# Revit family: 879-002X7X-001-DN200-400
name_source: partatom
category: Pipe Accessories
units: mm (PartAtom-declared; Revit-internal decimal feet)

## family parameters
Always vertical = Yes
Cut with Voids When Loaded = No
Part Type = Valve - Breaks Into
Round Connector Dimension = Use Diameter
Shared = No
Work Plane-Based = No

## types (80) — shared parameters
879-0200-00-04400207299 = DN200_PN10
879-0200-00-044002072A0 = DN200_PN10
879-0200-00-04400217299 = DN200_PN10
879-0200-00-044002172A0 = DN200_PN10
879-0200-00-04400227299 = DN200_PN10
879-0200-00-044002272A0 = DN200_PN10
879-0200-00-04400237299 = DN200_PN10
879-0200-00-044002372A0 = DN200_PN10
879-0200-00-14400207299 = DN200_PN16
879-0200-00-144002072A0 = DN200_PN16
879-0200-00-14400217299 = DN200_PN16
879-0200-00-144002172A0 = DN200_PN16
879-0200-00-14400227299 = DN200_PN16
879-0200-00-144002272A0 = DN200_PN16
879-0200-00-14400237299 = DN200_PN16
879-0200-00-144002372A0 = DN200_PN16
879-0250-00-04400207299 = DN250_PN10
879-0250-00-044002072A0 = DN250_PN10
879-0250-00-04400217299 = DN250_PN10
879-0250-00-044002172A0 = DN250_PN10
879-0250-00-04400227299 = DN250_PN10
879-0250-00-044002272A0 = DN250_PN10
879-0250-00-04400237299 = DN250_PN10
879-0250-00-044002372A0 = DN250_PN16
879-0250-00-14400207299 = DN250_PN16
879-0250-00-144002072A0 = DN250_PN16
879-0250-00-14400217299 = DN250_PN16
879-0250-00-144002172A0 = DN250_PN16
879-0250-00-14400227299 = DN250_PN16
879-0250-00-144002272A0 = DN250_PN16
879-0250-00-14400237299 = DN250_PN16
879-0250-00-144002372A0 = DN250_PN16
879-0300-00-04400207299 = DN300_PN10
879-0300-00-044002072A0 = DN300_PN10
879-0300-00-04400217299 = DN300_PN10
879-0300-00-044002172A0 = DN300_PN10
879-0300-00-04400227299 = DN300_PN10
879-0300-00-044002272A0 = DN300_PN10
879-0300-00-04400237299 = DN300_PN10
879-0300-00-044002372A0 = DN300_PN10
879-0300-00-14400207299 = DN300_PN16
879-0300-00-144002072A0 = DN300_PN16
879-0300-00-14400217299 = DN300_PN16
879-0300-00-144002172A0 = DN300_PN16
879-0300-00-14400227299 = DN300_PN16
879-0300-00-144002272A0 = DN300_PN16
879-0300-00-14400237299 = DN300_PN16
879-0300-00-144002372A0 = DN300_PN16
879-0350-00-04400207299 = DN350_PN10
879-0350-00-044002072A0 = DN350_PN10
879-0350-00-04400217299 = DN350_PN10
879-0350-00-044002172A0 = DN350_PN10
879-0350-00-04400227299 = DN350_PN10
879-0350-00-044002272A0 = DN350_PN10
879-0350-00-04400237299 = DN350_PN10
879-0350-00-044002372A0 = DN350_PN10
879-0350-00-14400207299 = DN350_PN16
879-0350-00-144002072A0 = DN350_PN16
879-0350-00-14400217299 = DN350_PN16
879-0350-00-144002172A0 = DN350_PN16
879-0350-00-14400227299 = DN350_PN16
879-0350-00-144002272A0 = DN350_PN16
879-0350-00-14400237299 = DN350_PN16
879-0350-00-144002372A0 = DN350_PN16
879-0400-00-04400207299 = DN400_PN10
879-0400-00-044002072A0 = DN400_PN10
879-0400-00-04400217299 = DN400_PN10
879-0400-00-044002172A0 = DN400_PN10
879-0400-00-04400227299 = DN400_PN10
879-0400-00-044002272A0 = DN400_PN10
879-0400-00-04400237299 = DN400_PN10
879-0400-00-044002372A0 = DN400_PN10
879-0400-00-14400207299 = DN400_PN16
879-0400-00-144002072A0 = DN400_PN16
879-0400-00-14400217299 = DN400_PN16
879-0400-00-144002172A0 = DN400_PN16
879-0400-00-14400227299 = DN400_PN16
879-0400-00-144002272A0 = DN400_PN16
879-0400-00-14400237299 = DN400_PN16
879-0400-00-144002372A0 = DN400_PN16
Body_wall_thickness = 10 mm  [stored 0.0328084 ft]
Description_ = AVK CONST. FLOW/PRESS. RED. CONTROL VALVE
Search_Table = 879-002X7X-001-DN200-400
URL product pages = https://www.avkvalves.com

## per-type parameters (varying)
- 879-0200-00-04400207299_DN200_PN10: A=194.55 mm; Body_Collar_Dia=62.5 mm; Body_Collar_Dia_2=30 mm  [stored 0.0984252 ft]; Body_Flange_Dia=157.89 mm; Body_Flange_Dia_2=162.16 mm; Body_Height_1=150 mm; Body_Height_2=75 mm; Body_Height_3=75 mm; Body_Height_4=90 mm; Body_Top_Dia=18.75 mm; Body_Top_Dia_2=15.63 mm; Body_With_Dia=133.33 mm; Body_With_Dia_2=133.33 mm; Bolt_support=352.94 mm; Bolt_support_2=176.47 mm; Bolt_support_Dia=20 mm  [stored 0.0656168 ft]; Bolt_support_lenght=120 mm; Bolt_support_lenght_2=130 mm; Bottom_profile=50 mm; D1=133 mm; DN=200 mm; FOD=170 mm; Fillet_Length=10 mm  [stored 0.0328084 ft]; Flange_thickness=20 mm  [stored 0.0656168 ft]; H3=615 mm; ID=100 mm; L=600 mm; L1=617 mm; L_Ref=608.5 mm; L_ref_2=265.71 mm; PG_Dia=80 mm; PG_Ref=100 mm; PG_depth=14 mm  [stored 0.0459318 ft]; PG_ref=110 mm; Pilot_Dia_1=38.5 mm; Pilot_Dia_1_Ref=46.2 mm; Pilot_Dia_1_Ref_2=92.4 mm; Pilot_Dia_2=65.45 mm; Pilot_Dia_3=25.67 mm; Pilot_Dia_4=12.83 mm; Pilot_Dia_5=8.56 mm; Pilot_top_1=390 mm; Pilot_top_ref=55 mm; Profile1_Height=273 mm; Profile1_Length=58.62 mm; Profile1_Length_2=39.08 mm; Profile_Dia=10 mm  [stored 0.0328084 ft]; Profile_Dia_2=10 mm  [stored 0.0328084 ft]; Profile_Dia_3=20 mm  [stored 0.0656168 ft]; Top_Profile=211.76 mm; Top_Profile_Ref=216.76 mm; Top_Ref=335 mm; Top_Ref_2=362.5 mm; W=425 mm; W_Ref=359.55 mm
- 879-0200-00-044002072A0_DN200_PN10: A=194.55 mm; Body_Collar_Dia=62.5 mm; Body_Collar_Dia_2=30 mm  [stored 0.0984252 ft]; Body_Flange_Dia=157.89 mm; Body_Flange_Dia_2=162.16 mm; Body_Height_1=150 mm; Body_Height_2=75 mm; Body_Height_3=100 mm; Body_Height_4=90 mm; Body_Top_Dia=18.75 mm; Body_Top_Dia_2=15.63 mm; Body_With_Dia=133.33 mm; Body_With_Dia_2=133.33 mm; Bolt_support=352.94 mm; Bolt_support_2=176.47 mm; Bolt_support_Dia=20 mm  [stored 0.0656168 ft]; Bolt_support_lenght=120.05 mm; Bolt_support_lenght_2=130.05 mm; Bottom_profile=50.03 mm; D1=133 mm; DN=200.1 mm; FOD=170 mm; Fillet_Length=10 mm  [stored 0.0328084 ft]; Flange_thickness=20 mm  [stored 0.0656168 ft]; H3=688 mm; ID=100.05 mm; L=600 mm; L1=617 mm; L_Ref=608.5 mm; L_ref_2=265.71 mm; PG_Dia=80 mm; PG_Ref=100 mm; PG_depth=14 mm  [stored 0.0459318 ft]; PG_ref=110.05 mm; Pilot_Dia_1=38.5 mm; Pilot_Dia_1_Ref=46.2 mm; Pilot_Dia_1_Ref_2=92.4 mm; Pilot_Dia_2=65.45 mm; Pilot_Dia_3=25.67 mm; Pilot_Dia_4=12.83 mm; Pilot_Dia_5=8.56 mm; Pilot_top_1=439 mm; Pilot_top_ref=79 mm; Profile1_Height=275 mm; Profile1_Length=58.62 mm; Profile1_Length_2=39.08 mm; Profile_Dia=10 mm  [stored 0.0328084 ft]; Profile_Dia_2=10 mm  [stored 0.0328084 ft]; Profile_Dia_3=20 mm  [stored 0.0656168 ft]; Top_Profile=211.76 mm; Top_Profile_Ref=216.76 mm; Top_Ref=360 mm; Top_Ref_2=399.5 mm; W=425 mm; W_Ref=359.55 mm
- 879-0200-00-04400217299_DN200_PN10: A=194.55 mm; Body_Collar_Dia=62.5 mm; Body_Collar_Dia_2=30 mm  [stored 0.0984252 ft]; Body_Flange_Dia=157.89 mm; Body_Flange_Dia_2=162.16 mm; Body_Height_1=150 mm; Body_Height_2=75 mm; Body_Height_3=75 mm; Body_Height_4=90 mm; Body_Top_Dia=18.75 mm; Body_Top_Dia_2=15.63 mm; Body_With_Dia=133.33 mm; Body_With_Dia_2=133.33 mm; Bolt_support=352.94 mm; Bolt_support_2=176.47 mm; Bolt_support_Dia=20 mm  [stored 0.0656168 ft]; Bolt_support_lenght=120.1 mm; Bolt_support_lenght_2=130.1 mm; Bottom_profile=50.05 mm; D1=133 mm; DN=200.2 mm; FOD=170 mm; Fillet_Length=10 mm  [stored 0.0328084 ft]; Flange_thickness=20 mm  [stored 0.0656168 ft]; H3=615 mm; ID=100.1 mm; L=600 mm; L1=617 mm; L_Ref=608.5 mm; L_ref_2=265.71 mm; PG_Dia=80 mm; PG_Ref=100 mm; PG_depth=14 mm  [stored 0.0459318 ft]; PG_ref=110.1 mm; Pilot_Dia_1=38.5 mm; Pilot_Dia_1_Ref=46.2 mm; Pilot_Dia_1_Ref_2=92.4 mm; Pilot_Dia_2=65.45 mm; Pilot_Dia_3=25.67 mm; Pilot_Dia_4=12.83 mm; Pilot_Dia_5=8.56 mm; Pilot_top_1=390 mm; Pilot_top_ref=55 mm; Profile1_Height=273 mm; Profile1_Length=58.62 mm; Profile1_Length_2=39.08 mm; Profile_Dia=10 mm  [stored 0.0328084 ft]; Profile_Dia_2=10 mm  [stored 0.0328084 ft]; Profile_Dia_3=20 mm  [stored 0.0656168 ft]; Top_Profile=211.76 mm; Top_Profile_Ref=216.76 mm; Top_Ref=335 mm; Top_Ref_2=362.5 mm; W=425 mm; W_Ref=359.55 mm
- 879-0200-00-044002172A0_DN200_PN10: A=194.55 mm; Body_Collar_Dia=62.5 mm; Body_Collar_Dia_2=30 mm  [stored 0.0984252 ft]; Body_Flange_Dia=157.89 mm; Body_Flange_Dia_2=162.16 mm; Body_Height_1=150 mm; Body_Height_2=75 mm; Body_Height_3=86 mm; Body_Height_4=90 mm; Body_Top_Dia=18.75 mm; Body_Top_Dia_2=15.63 mm; Body_With_Dia=133.33 mm; Body_With_Dia_2=133.33 mm; Bolt_support=352.94 mm; Bolt_support_2=176.47 mm; Bolt_support_Dia=20 mm  [stored 0.0656168 ft]; Bolt_support_lenght=120.15 mm; Bolt_support_lenght_2=130.15 mm; Bottom_profile=50.08 mm; D1=133 mm; DN=200.3 mm; FOD=170 mm; Fillet_Length=10 mm  [stored 0.0328084 ft]; Flange_thickness=20 mm  [stored 0.0656168 ft]; H3=688 mm; ID=100.15 mm; L=600 mm; L1=617 mm; L_Ref=608.5 mm; L_ref_2=265.71 mm; PG_Dia=80 mm; PG_Ref=100 mm; PG_depth=14 mm  [stored 0.0459318 ft]; PG_ref=110.15 mm; Pilot_Dia_1=38.5 mm; Pilot_Dia_1_Ref=46.2 mm; Pilot_Dia_1_Ref_2=92.4 mm; Pilot_Dia_2=65.45 mm; Pilot_Dia_3=25.67 mm; Pilot_Dia_4=12.83 mm; Pilot_Dia_5=8.56 mm; Pilot_top_1=432 mm; Pilot_top_ref=86 mm; Profile1_Height=275 mm; Profile1_Length=58.62 mm; Profile1_Length_2=39.08 mm; Profile_Dia=10 mm  [stored 0.0328084 ft]; Profile_Dia_2=10 mm  [stored 0.0328084 ft]; Profile_Dia_3=20 mm  [stored 0.0656168 ft]; Top_Profile=211.76 mm; Top_Profile_Ref=216.76 mm; Top_Ref=346 mm; Top_Ref_2=389 mm; W=425 mm; W_Ref=359.55 mm
- 879-0200-00-04400227299_DN200_PN10: A=194.55 mm; Body_Collar_Dia=62.5 mm; Body_Collar_Dia_2=30 mm  [stored 0.0984252 ft]; Body_Flange_Dia=157.89 mm; Body_Flange_Dia_2=162.16 mm; Body_Height_1=150 mm; Body_Height_2=75 mm; Body_Height_3=75 mm; Body_Height_4=90 mm; Body_Top_Dia=18.75 mm; Body_Top_Dia_2=15.63 mm; Body_With_Dia=133.33 mm; Body_With_Dia_2=133.33 mm; Bolt_support=352.94 mm; Bolt_support_2=176.47 mm; Bolt_support_Dia=20 mm  [stored 0.0656168 ft]; Bolt_support_lenght=120.2 mm; Bolt_support_lenght_2=130.2 mm; Bottom_profile=50.1 mm; D1=133 mm; DN=200.4 mm; FOD=170 mm; Fillet_Length=10 mm  [stored 0.0328084 ft]; Flange_thickness=20 mm  [stored 0.0656168 ft]; H3=615 mm; ID=100.2 mm; L=600 mm; L1=617 mm; L_Ref=608.5 mm; L_ref_2=265.71 mm; PG_Dia=80 mm; PG_Ref=100 mm; PG_depth=14 mm  [stored 0.0459318 ft]; PG_ref=110.2 mm; Pilot_Dia_1=38.5 mm; Pilot_Dia_1_Ref=46.2 mm; Pilot_Dia_1_Ref_2=92.4 mm; Pilot_Dia_2=65.45 mm; Pilot_Dia_3=25.67 mm; Pilot_Dia_4=12.83 mm; Pilot_Dia_5=8.56 mm; Pilot_top_1=390 mm; Pilot_top_ref=55 mm; Profile1_Height=273 mm; Profile1_Length=58.62 mm; Profile1_Length_2=39.08 mm; Profile_Dia=10 mm  [stored 0.0328084 ft]; Profile_Dia_2=10 mm  [stored 0.0328084 ft]; Profile_Dia_3=20 mm  [stored 0.0656168 ft]; Top_Profile=211.76 mm; Top_Profile_Ref=216.76 mm; Top_Ref=335 mm; Top_Ref_2=362.5 mm; W=425 mm; W_Ref=359.55 mm
- 879-0200-00-044002272A0_DN200_PN10: A=194.55 mm; Body_Collar_Dia=62.5 mm; Body_Collar_Dia_2=30 mm  [stored 0.0984252 ft]; Body_Flange_Dia=157.89 mm; Body_Flange_Dia_2=162.16 mm; Body_Height_1=150 mm; Body_Height_2=75 mm; Body_Height_3=100 mm; Body_Height_4=90 mm; Body_Top_Dia=18.75 mm; Body_Top_Dia_2=15.63 mm; Body_With_Dia=133.33 mm; Body_With_Dia_2=133.33 mm; Bolt_support=352.94 mm; Bolt_support_2=176.47 mm; Bolt_support_Dia=20 mm  [stored 0.0656168 ft]; Bolt_support_lenght=120.25 mm; Bolt_support_lenght_2=130.25 mm; Bottom_profile=50.13 mm; D1=133 mm; DN=200.5 mm; FOD=170 mm; Fillet_Length=10 mm  [stored 0.0328084 ft]; Flange_thickness=20 mm  [stored 0.0656168 ft]; H3=688 mm; ID=100.25 mm; L=600 mm; L1=617 mm; L_Ref=608.5 mm; L_ref_2=265.71 mm; PG_Dia=80 mm; PG_Ref=100 mm; PG_depth=14 mm  [stored 0.0459318 ft]; PG_ref=110.25 mm; Pilot_Dia_1=38.5 mm; Pilot_Dia_1_Ref=46.2 mm; Pilot_Dia_1_Ref_2=92.4 mm; Pilot_Dia_2=65.45 mm; Pilot_Dia_3=25.67 mm; Pilot_Dia_4=12.83 mm; Pilot_Dia_5=8.56 mm; Pilot_top_1=439 mm; Pilot_top_ref=79 mm; Profile1_Height=275 mm; Profile1_Length=58.62 mm; Profile1_Length_2=39.08 mm; Profile_Dia=10 mm  [stored 0.0328084 ft]; Profile_Dia_2=10 mm  [stored 0.0328084 ft]; Profile_Dia_3=20 mm  [stored 0.0656168 ft]; Top_Profile=211.76 mm; Top_Profile_Ref=216.76 mm; Top_Ref=360 mm; Top_Ref_2=399.5 mm; W=425 mm; W_Ref=359.55 mm
- 879-0200-00-04400237299_DN200_PN10: A=194.55 mm; Body_Collar_Dia=62.5 mm; Body_Collar_Dia_2=30 mm  [stored 0.0984252 ft]; Body_Flange_Dia=157.89 mm; Body_Flange_Dia_2=162.16 mm; Body_Height_1=150 mm; Body_Height_2=75 mm; Body_Height_3=75 mm; Body_Height_4=90 mm; Body_Top_Dia=18.75 mm; Body_Top_Dia_2=15.63 mm; Body_With_Dia=133.33 mm; Body_With_Dia_2=133.33 mm; Bolt_support=352.94 mm; Bolt_support_2=176.47 mm; Bolt_support_Dia=20 mm  [stored 0.0656168 ft]; Bolt_support_lenght=120.3 mm; Bolt_support_lenght_2=130.3 mm; Bottom_profile=50.15 mm; D1=133 mm; DN=200.6 mm; FOD=170 mm; Fillet_Length=10 mm  [stored 0.0328084 ft]; Flange_thickness=20 mm  [stored 0.0656168 ft]; H3=615 mm; ID=100.3 mm; L=600 mm; L1=617 mm; L_Ref=608.5 mm; L_ref_2=265.71 mm; PG_Dia=80 mm; PG_Ref=100 mm; PG_depth=14 mm  [stored 0.0459318 ft]; PG_ref=110.3 mm; Pilot_Dia_1=38.5 mm; Pilot_Dia_1_Ref=46.2 mm; Pilot_Dia_1_Ref_2=92.4 mm; Pilot_Dia_2=65.45 mm; Pilot_Dia_3=25.67 mm; Pilot_Dia_4=12.83 mm; Pilot_Dia_5=8.56 mm; Pilot_top_1=390 mm; Pilot_top_ref=55 mm; Profile1_Height=273 mm; Profile1_Length=58.62 mm; Profile1_Length_2=39.08 mm; Profile_Dia=10 mm  [stored 0.0328084 ft]; Profile_Dia_2=10 mm  [stored 0.0328084 ft]; Profile_Dia_3=20 mm  [stored 0.0656168 ft]; Top_Profile=211.76 mm; Top_Profile_Ref=216.76 mm; Top_Ref=335 mm; Top_Ref_2=362.5 mm; W=425 mm; W_Ref=359.55 mm
- 879-0200-00-044002372A0_DN200_PN10: A=194.55 mm; Body_Collar_Dia=62.5 mm; Body_Collar_Dia_2=30 mm  [stored 0.0984252 ft]; Body_Flange_Dia=157.89 mm; Body_Flange_Dia_2=162.16 mm; Body_Height_1=150 mm; Body_Height_2=75 mm; Body_Height_3=86 mm; Body_Height_4=90 mm; Body_Top_Dia=18.75 mm; Body_Top_Dia_2=15.63 mm; Body_With_Dia=133.33 mm; Body_With_Dia_2=133.33 mm; Bolt_support=352.94 mm; Bolt_support_2=176.47 mm; Bolt_support_Dia=20 mm  [stored 0.0656168 ft]; Bolt_support_lenght=120.35 mm; Bolt_support_lenght_2=130.35 mm; Bottom_profile=50.18 mm; D1=133 mm; DN=200.7 mm; FOD=170 mm; Fillet_Length=10 mm  [stored 0.0328084 ft]; Flange_thickness=20 mm  [stored 0.0656168 ft]; H3=688 mm; ID=100.35 mm; L=600 mm; L1=617 mm; L_Ref=608.5 mm; L_ref_2=265.71 mm; PG_Dia=80 mm; PG_Ref=100 mm; PG_depth=14 mm  [stored 0.0459318 ft]; PG_ref=110.35 mm; Pilot_Dia_1=38.5 mm; Pilot_Dia_1_Ref=46.2 mm; Pilot_Dia_1_Ref_2=92.4 mm; Pilot_Dia_2=65.45 mm; Pilot_Dia_3=25.67 mm; Pilot_Dia_4=12.83 mm; Pilot_Dia_5=8.56 mm; Pilot_top_1=432 mm; Pilot_top_ref=86 mm; Profile1_Height=275 mm; Profile1_Length=58.62 mm; Profile1_Length_2=39.08 mm; Profile_Dia=10 mm  [stored 0.0328084 ft]; Profile_Dia_2=10 mm  [stored 0.0328084 ft]; Profile_Dia_3=20 mm  [stored 0.0656168 ft]; Top_Profile=211.76 mm; Top_Profile_Ref=216.76 mm; Top_Ref=346 mm; Top_Ref_2=389 mm; W=425 mm; W_Ref=359.55 mm
- 879-0200-00-14400207299_DN200_PN16: A=194.55 mm; Body_Collar_Dia=62.5 mm; Body_Collar_Dia_2=30 mm  [stored 0.0984252 ft]; Body_Flange_Dia=157.89 mm; Body_Flange_Dia_2=162.16 mm; Body_Height_1=150 mm; Body_Height_2=75 mm; Body_Height_3=75 mm; Body_Height_4=90 mm; Body_Top_Dia=18.75 mm; Body_Top_Dia_2=15.63 mm; Body_With_Dia=133.33 mm; Body_With_Dia_2=133.33 mm; Bolt_support=352.94 mm; Bolt_support_2=176.47 mm; Bolt_support_Dia=20 mm  [stored 0.0656168 ft]; Bolt_support_lenght=120.4 mm; Bolt_support_lenght_2=130.4 mm; Bottom_profile=50.2 mm; D1=133 mm; DN=200.8 mm; FOD=170 mm; Fillet_Length=10 mm  [stored 0.0328084 ft]; Flange_thickness=20 mm  [stored 0.0656168 ft]; H3=615 mm; ID=100.4 mm; L=600 mm; L1=617 mm; L_Ref=608.5 mm; L_ref_2=265.71 mm; PG_Dia=80 mm; PG_Ref=100 mm; PG_depth=14 mm  [stored 0.0459318 ft]; PG_ref=110.4 mm; Pilot_Dia_1=38.5 mm; Pilot_Dia_1_Ref=46.2 mm; Pilot_Dia_1_Ref_2=92.4 mm; Pilot_Dia_2=65.45 mm; Pilot_Dia_3=25.67 mm; Pilot_Dia_4=12.83 mm; Pilot_Dia_5=8.56 mm; Pilot_top_1=390 mm; Pilot_top_ref=55 mm; Profile1_Height=273 mm; Profile1_Length=58.62 mm; Profile1_Length_2=39.08 mm; Profile_Dia=10 mm  [stored 0.0328084 ft]; Profile_Dia_2=10 mm  [stored 0.0328084 ft]; Profile_Dia_3=20 mm  [stored 0.0656168 ft]; Top_Profile=211.76 mm; Top_Profile_Ref=216.76 mm; Top_Ref=335 mm; Top_Ref_2=362.5 mm; W=425 mm; W_Ref=359.55 mm
- 879-0200-00-144002072A0_DN200_PN16: A=194.55 mm; Body_Collar_Dia=62.5 mm; Body_Collar_Dia_2=30 mm  [stored 0.0984252 ft]; Body_Flange_Dia=157.89 mm; Body_Flange_Dia_2=162.16 mm; Body_Height_1=150 mm; Body_Height_2=75 mm; Body_Height_3=100 mm; Body_Height_4=90 mm; Body_Top_Dia=18.75 mm; Body_Top_Dia_2=15.63 mm; Body_With_Dia=133.33 mm; Body_With_Dia_2=133.33 mm; Bolt_support=352.94 mm; Bolt_support_2=176.47 mm; Bolt_support_Dia=20 mm  [stored 0.0656168 ft]; Bolt_support_lenght=120.45 mm; Bolt_support_lenght_2=130.45 mm; Bottom_profile=50.23 mm; D1=133 mm; DN=200.9 mm; FOD=170 mm; Fillet_Length=10 mm  [stored 0.0328084 ft]; Flange_thickness=20 mm  [stored 0.0656168 ft]; H3=688 mm; ID=100.45 mm; L=600 mm; L1=617 mm; L_Ref=608.5 mm; L_ref_2=265.71 mm; PG_Dia=80 mm; PG_Ref=100 mm; PG_depth=14 mm  [stored 0.0459318 ft]; PG_ref=110.45 mm; Pilot_Dia_1=38.5 mm; Pilot_Dia_1_Ref=46.2 mm; Pilot_Dia_1_Ref_2=92.4 mm; Pilot_Dia_2=65.45 mm; Pilot_Dia_3=25.67 mm; Pilot_Dia_4=12.83 mm; Pilot_Dia_5=8.56 mm; Pilot_top_1=439 mm; Pilot_top_ref=79 mm; Profile1_Height=275 mm; Profile1_Length=58.62 mm; Profile1_Length_2=39.08 mm; Profile_Dia=10 mm  [stored 0.0328084 ft]; Profile_Dia_2=10 mm  [stored 0.0328084 ft]; Profile_Dia_3=20 mm  [stored 0.0656168 ft]; Top_Profile=211.76 mm; Top_Profile_Ref=216.76 mm; Top_Ref=360 mm; Top_Ref_2=399.5 mm; W=425 mm; W_Ref=359.55 mm
- 879-0200-00-14400217299_DN200_PN16: A=194.55 mm; Body_Collar_Dia=62.5 mm; Body_Collar_Dia_2=30 mm  [stored 0.0984252 ft]; Body_Flange_Dia=157.89 mm; Body_Flange_Dia_2=162.16 mm; Body_Height_1=150 mm; Body_Height_2=75 mm; Body_Height_3=75 mm; Body_Height_4=90 mm; Body_Top_Dia=18.75 mm; Body_Top_Dia_2=15.63 mm; Body_With_Dia=133.33 mm; Body_With_Dia_2=133.33 mm; Bolt_support=352.94 mm; Bolt_support_2=176.47 mm; Bolt_support_Dia=20 mm  [stored 0.0656168 ft]; Bolt_support_lenght=120.06 mm; Bolt_support_lenght_2=130.06 mm; Bottom_profile=50.03 mm; D1=133 mm; DN=200.11 mm; FOD=170 mm; Fillet_Length=10 mm  [stored 0.0328084 ft]; Flange_thickness=20 mm  [stored 0.0656168 ft]; H3=615 mm; ID=100.06 mm; L=600 mm; L1=617 mm; L_Ref=608.5 mm; L_ref_2=265.71 mm; PG_Dia=80 mm; PG_Ref=100 mm; PG_depth=14 mm  [stored 0.0459318 ft]; PG_ref=110.06 mm; Pilot_Dia_1=38.5 mm; Pilot_Dia_1_Ref=46.2 mm; Pilot_Dia_1_Ref_2=92.4 mm; Pilot_Dia_2=65.45 mm; Pilot_Dia_3=25.67 mm; Pilot_Dia_4=12.83 mm; Pilot_Dia_5=8.56 mm; Pilot_top_1=390 mm; Pilot_top_ref=55 mm; Profile1_Height=273 mm; Profile1_Length=58.62 mm; Profile1_Length_2=39.08 mm; Profile_Dia=10 mm  [stored 0.0328084 ft]; Profile_Dia_2=10 mm  [stored 0.0328084 ft]; Profile_Dia_3=20 mm  [stored 0.0656168 ft]; Top_Profile=211.76 mm; Top_Profile_Ref=216.76 mm; Top_Ref=335 mm; Top_Ref_2=362.5 mm; W=425 mm; W_Ref=359.55 mm
- 879-0200-00-144002172A0_DN200_PN16: A=194.55 mm; Body_Collar_Dia=62.5 mm; Body_Collar_Dia_2=30 mm  [stored 0.0984252 ft]; Body_Flange_Dia=157.89 mm; Body_Flange_Dia_2=162.16 mm; Body_Height_1=150 mm; Body_Height_2=75 mm; Body_Height_3=86 mm; Body_Height_4=90 mm; Body_Top_Dia=18.75 mm; Body_Top_Dia_2=15.63 mm; Body_With_Dia=133.33 mm; Body_With_Dia_2=133.33 mm; Bolt_support=352.94 mm; Bolt_support_2=176.47 mm; Bolt_support_Dia=20 mm  [stored 0.0656168 ft]; Bolt_support_lenght=120.06 mm; Bolt_support_lenght_2=130.06 mm; Bottom_profile=50.03 mm; D1=133 mm; DN=200.12 mm; FOD=170 mm; Fillet_Length=10 mm  [stored 0.0328084 ft]; Flange_thickness=20 mm  [stored 0.0656168 ft]; H3=688 mm; ID=100.06 mm; L=600 mm; L1=617 mm; L_Ref=608.5 mm; L_ref_2=265.71 mm; PG_Dia=80 mm; PG_Ref=100 mm; PG_depth=14 mm  [stored 0.0459318 ft]; PG_ref=110.06 mm; Pilot_Dia_1=38.5 mm; Pilot_Dia_1_Ref=46.2 mm; Pilot_Dia_1_Ref_2=92.4 mm; Pilot_Dia_2=65.45 mm; Pilot_Dia_3=25.67 mm; Pilot_Dia_4=12.83 mm; Pilot_Dia_5=8.56 mm; Pilot_top_1=432 mm; Pilot_top_ref=86 mm; Profile1_Height=275 mm; Profile1_Length=58.62 mm; Profile1_Length_2=39.08 mm; Profile_Dia=10 mm  [stored 0.0328084 ft]; Profile_Dia_2=10 mm  [stored 0.0328084 ft]; Profile_Dia_3=20 mm  [stored 0.0656168 ft]; Top_Profile=211.76 mm; Top_Profile_Ref=216.76 mm; Top_Ref=346 mm; Top_Ref_2=389 mm; W=425 mm; W_Ref=359.55 mm
- 879-0200-00-14400227299_DN200_PN16: A=194.55 mm; Body_Collar_Dia=62.5 mm; Body_Collar_Dia_2=30 mm  [stored 0.0984252 ft]; Body_Flange_Dia=157.89 mm; Body_Flange_Dia_2=162.16 mm; Body_Height_1=150 mm; Body_Height_2=75 mm; Body_Height_3=75 mm; Body_Height_4=90 mm; Body_Top_Dia=18.75 mm; Body_Top_Dia_2=15.63 mm; Body_With_Dia=133.33 mm; Body_With_Dia_2=133.33 mm; Bolt_support=352.94 mm; Bolt_support_2=176.47 mm; Bolt_support_Dia=20 mm  [stored 0.0656168 ft]; Bolt_support_lenght=120.07 mm; Bolt_support_lenght_2=130.07 mm; Bottom_profile=50.03 mm; D1=133 mm; DN=200.13 mm; FOD=170 mm; Fillet_Length=10 mm  [stored 0.0328084 ft]; Flange_thickness=20 mm  [stored 0.0656168 ft]; H3=615 mm; ID=100.07 mm; L=600 mm; L1=617 mm; L_Ref=608.5 mm; L_ref_2=265.71 mm; PG_Dia=80 mm; PG_Ref=100 mm; PG_depth=14 mm  [stored 0.0459318 ft]; PG_ref=110.07 mm; Pilot_Dia_1=38.5 mm; Pilot_Dia_1_Ref=46.2 mm; Pilot_Dia_1_Ref_2=92.4 mm; Pilot_Dia_2=65.45 mm; Pilot_Dia_3=25.67 mm; Pilot_Dia_4=12.83 mm; Pilot_Dia_5=8.56 mm; Pilot_top_1=390 mm; Pilot_top_ref=55 mm; Profile1_Height=273 mm; Profile1_Length=58.62 mm; Profile1_Length_2=39.08 mm; Profile_Dia=10 mm  [stored 0.0328084 ft]; Profile_Dia_2=10 mm  [stored 0.0328084 ft]; Profile_Dia_3=20 mm  [stored 0.0656168 ft]; Top_Profile=211.76 mm; Top_Profile_Ref=216.76 mm; Top_Ref=335 mm; Top_Ref_2=362.5 mm; W=425 mm; W_Ref=359.55 mm
- 879-0200-00-144002272A0_DN200_PN16: A=194.55 mm; Body_Collar_Dia=62.5 mm; Body_Collar_Dia_2=30 mm  [stored 0.0984252 ft]; Body_Flange_Dia=157.89 mm; Body_Flange_Dia_2=162.16 mm; Body_Height_1=150 mm; Body_Height_2=75 mm; Body_Height_3=100 mm; Body_Height_4=90 mm; Body_Top_Dia=18.75 mm; Body_Top_Dia_2=15.63 mm; Body_With_Dia=133.33 mm; Body_With_Dia_2=133.33 mm; Bolt_support=352.94 mm; Bolt_support_2=176.47 mm; Bolt_support_Dia=20 mm  [stored 0.0656168 ft]; Bolt_support_lenght=120.07 mm; Bolt_support_lenght_2=130.07 mm; Bottom_profile=50.04 mm; D1=133 mm; DN=200.14 mm; FOD=170 mm; Fillet_Length=10 mm  [stored 0.0328084 ft]; Flange_thickness=20 mm  [stored 0.0656168 ft]; H3=688 mm; ID=100.07 mm; L=600 mm; L1=617 mm; L_Ref=608.5 mm; L_ref_2=265.71 mm; PG_Dia=80 mm; PG_Ref=100 mm; PG_depth=14 mm  [stored 0.0459318 ft]; PG_ref=110.07 mm; Pilot_Dia_1=38.5 mm; Pilot_Dia_1_Ref=46.2 mm; Pilot_Dia_1_Ref_2=92.4 mm; Pilot_Dia_2=65.45 mm; Pilot_Dia_3=25.67 mm; Pilot_Dia_4=12.83 mm; Pilot_Dia_5=8.56 mm; Pilot_top_1=439 mm; Pilot_top_ref=79 mm; Profile1_Height=275 mm; Profile1_Length=58.62 mm; Profile1_Length_2=39.08 mm; Profile_Dia=10 mm  [stored 0.0328084 ft]; Profile_Dia_2=10 mm  [stored 0.0328084 ft]; Profile_Dia_3=20 mm  [stored 0.0656168 ft]; Top_Profile=211.76 mm; Top_Profile_Ref=216.76 mm; Top_Ref=360 mm; Top_Ref_2=399.5 mm; W=425 mm; W_Ref=359.55 mm
- 879-0200-00-14400237299_DN200_PN16: A=194.55 mm; Body_Collar_Dia=62.5 mm; Body_Collar_Dia_2=30 mm  [stored 0.0984252 ft]; Body_Flange_Dia=157.89 mm; Body_Flange_Dia_2=162.16 mm; Body_Height_1=150 mm; Body_Height_2=75 mm; Body_Height_3=75 mm; Body_Height_4=90 mm; Body_Top_Dia=18.75 mm; Body_Top_Dia_2=15.63 mm; Body_With_Dia=133.33 mm; Body_With_Dia_2=133.33 mm; Bolt_support=352.94 mm; Bolt_support_2=176.47 mm; Bolt_support_Dia=20 mm  [stored 0.0656168 ft]; Bolt_support_lenght=120.08 mm; Bolt_support_lenght_2=130.08 mm; Bottom_profile=50.04 mm; D1=133 mm; DN=200.15 mm; FOD=170 mm; Fillet_Length=10 mm  [stored 0.0328084 ft]; Flange_thickness=20 mm  [stored 0.0656168 ft]; H3=615 mm; ID=100.08 mm; L=600 mm; L1=617 mm; L_Ref=608.5 mm; L_ref_2=265.71 mm; PG_Dia=80 mm; PG_Ref=100 mm; PG_depth=14 mm  [stored 0.0459318 ft]; PG_ref=110.08 mm; Pilot_Dia_1=38.5 mm; Pilot_Dia_1_Ref=46.2 mm; Pilot_Dia_1_Ref_2=92.4 mm; Pilot_Dia_2=65.45 mm; Pilot_Dia_3=25.67 mm; Pilot_Dia_4=12.83 mm; Pilot_Dia_5=8.56 mm; Pilot_top_1=390 mm; Pilot_top_ref=55 mm; Profile1_Height=273 mm; Profile1_Length=58.62 mm; Profile1_Length_2=39.08 mm; Profile_Dia=10 mm  [stored 0.0328084 ft]; Profile_Dia_2=10 mm  [stored 0.0328084 ft]; Profile_Dia_3=20 mm  [stored 0.0656168 ft]; Top_Profile=211.76 mm; Top_Profile_Ref=216.76 mm; Top_Ref=335 mm; Top_Ref_2=362.5 mm; W=425 mm; W_Ref=359.55 mm
- 879-0200-00-144002372A0_DN200_PN16: A=194.55 mm; Body_Collar_Dia=62.5 mm; Body_Collar_Dia_2=30 mm  [stored 0.0984252 ft]; Body_Flange_Dia=157.89 mm; Body_Flange_Dia_2=162.16 mm; Body_Height_1=150 mm; Body_Height_2=75 mm; Body_Height_3=86 mm; Body_Height_4=90 mm; Body_Top_Dia=18.75 mm; Body_Top_Dia_2=15.63 mm; Body_With_Dia=133.33 mm; Body_With_Dia_2=133.33 mm; Bolt_support=352.94 mm; Bolt_support_2=176.47 mm; Bolt_support_Dia=20 mm  [stored 0.0656168 ft]; Bolt_support_lenght=120.08 mm; Bolt_support_lenght_2=130.08 mm; Bottom_profile=50.04 mm; D1=133 mm; DN=200.16 mm; FOD=170 mm; Fillet_Length=10 mm  [stored 0.0328084 ft]; Flange_thickness=20 mm  [stored 0.0656168 ft]; H3=688 mm; ID=100.08 mm; L=600 mm; L1=617 mm; L_Ref=608.5 mm; L_ref_2=265.71 mm; PG_Dia=80 mm; PG_Ref=100 mm; PG_depth=14 mm  [stored 0.0459318 ft]; PG_ref=110.08 mm; Pilot_Dia_1=38.5 mm; Pilot_Dia_1_Ref=46.2 mm; Pilot_Dia_1_Ref_2=92.4 mm; Pilot_Dia_2=65.45 mm; Pilot_Dia_3=25.67 mm; Pilot_Dia_4=12.83 mm; Pilot_Dia_5=8.56 mm; Pilot_top_1=432 mm; Pilot_top_ref=86 mm; Profile1_Height=275 mm; Profile1_Length=58.62 mm; Profile1_Length_2=39.08 mm; Profile_Dia=10 mm  [stored 0.0328084 ft]; Profile_Dia_2=10 mm  [stored 0.0328084 ft]; Profile_Dia_3=20 mm  [stored 0.0656168 ft]; Top_Profile=211.76 mm; Top_Profile_Ref=216.76 mm; Top_Ref=346 mm; Top_Ref_2=389 mm; W=425 mm; W_Ref=359.55 mm
- 879-0250-00-04400207299_DN250_PN10: A=239.3 mm; Body_Collar_Dia=76.04 mm; Body_Collar_Dia_2=36.5 mm; Body_Flange_Dia=192.11 mm; Body_Flange_Dia_2=197.3 mm; Body_Height_1=182.5 mm; Body_Height_2=91.25 mm; Body_Height_3=81 mm; Body_Height_4=106.25 mm; Body_Top_Dia=22.81 mm; Body_Top_Dia_2=19.01 mm; Body_With_Dia=162.22 mm; Body_With_Dia_2=162.22 mm; Bolt_support=429.41 mm; Bolt_support_2=214.71 mm; Bolt_support_Dia=20 mm  [stored 0.0656168 ft]; Bolt_support_lenght=145 mm; Bolt_support_lenght_2=155 mm; Bottom_profile=62.5 mm; D1=159.5 mm; DN=250 mm; FOD=197.5 mm; Fillet_Length=10 mm  [stored 0.0328084 ft]; Flange_thickness=22 mm  [stored 0.0721785 ft]; H3=720 mm; ID=125 mm; L=730 mm; L1=747 mm; L_Ref=738.5 mm; L_ref_2=325.62 mm; PG_Dia=80 mm; PG_Ref=121.67 mm; PG_depth=14 mm  [stored 0.0459318 ft]; PG_ref=135 mm; Pilot_Dia_1=46 mm; Pilot_Dia_1_Ref=55.2 mm; Pilot_Dia_1_Ref_2=110.4 mm; Pilot_Dia_2=78.2 mm; Pilot_Dia_3=30.67 mm; Pilot_Dia_4=15.33 mm; Pilot_Dia_5=10.22 mm; Pilot_top_1=456.13 mm; Pilot_top_ref=66.38 mm; Profile1_Height=327 mm; Profile1_Length=68.1 mm; Profile1_Length_2=45.4 mm; Profile_Dia=10 mm  [stored 0.0328084 ft]; Profile_Dia_2=10 mm  [stored 0.0328084 ft]; Profile_Dia_3=20 mm  [stored 0.0656168 ft]; Top_Profile=257.65 mm; Top_Profile_Ref=262.65 mm; Top_Ref=389.75 mm; Top_Ref_2=422.94 mm; W=510 mm; W_Ref=431.8 mm
- 879-0250-00-044002072A0_DN250_PN10: A=239.3 mm; Body_Collar_Dia=76.04 mm; Body_Collar_Dia_2=36.5 mm; Body_Flange_Dia=192.11 mm; Body_Flange_Dia_2=197.3 mm; Body_Height_1=182.5 mm; Body_Height_2=91.25 mm; Body_Height_3=104.5 mm; Body_Height_4=106.25 mm; Body_Top_Dia=22.81 mm; Body_Top_Dia_2=19.01 mm; Body_With_Dia=162.22 mm; Body_With_Dia_2=162.22 mm; Bolt_support=429.41 mm; Bolt_support_2=214.71 mm; Bolt_support_Dia=20 mm  [stored 0.0656168 ft]; Bolt_support_lenght=145.05 mm; Bolt_support_lenght_2=155.05 mm; Bottom_profile=62.53 mm; D1=159.5 mm; DN=250.1 mm; FOD=197.5 mm; Fillet_Length=10 mm  [stored 0.0328084 ft]; Flange_thickness=22 mm  [stored 0.0721785 ft]; H3=806 mm; ID=125.05 mm; L=730 mm; L1=747 mm; L_Ref=738.5 mm; L_ref_2=325.62 mm; PG_Dia=80 mm; PG_Ref=121.67 mm; PG_depth=14 mm  [stored 0.0459318 ft]; PG_ref=135.05 mm; Pilot_Dia_1=46 mm; Pilot_Dia_1_Ref=55.2 mm; Pilot_Dia_1_Ref_2=110.4 mm; Pilot_Dia_2=78.2 mm; Pilot_Dia_3=30.67 mm; Pilot_Dia_4=15.33 mm; Pilot_Dia_5=10.22 mm; Pilot_top_1=510.88 mm; Pilot_top_ref=97.63 mm; Profile1_Height=330 mm; Profile1_Length=68.1 mm; Profile1_Length_2=45.4 mm; Profile_Dia=10 mm  [stored 0.0328084 ft]; Profile_Dia_2=10 mm  [stored 0.0328084 ft]; Profile_Dia_3=20 mm  [stored 0.0656168 ft]; Top_Profile=257.65 mm; Top_Profile_Ref=262.65 mm; Top_Ref=413.25 mm; Top_Ref_2=462.06 mm; W=510 mm; W_Ref=431.8 mm
- 879-0250-00-04400217299_DN250_PN10: A=237.6 mm; Body_Collar_Dia=76.04 mm; Body_Collar_Dia_2=36.5 mm; Body_Flange_Dia=192.11 mm; Body_Flange_Dia_2=197.3 mm; Body_Height_1=182.5 mm; Body_Height_2=91.25 mm; Body_Height_3=81 mm; Body_Height_4=106.25 mm; Body_Top_Dia=22.81 mm; Body_Top_Dia_2=19.01 mm; Body_With_Dia=162.22 mm; Body_With_Dia_2=162.22 mm; Bolt_support=429.41 mm; Bolt_support_2=214.71 mm; Bolt_support_Dia=20 mm  [stored 0.0656168 ft]; Bolt_support_lenght=145.1 mm; Bolt_support_lenght_2=155.1 mm; Bottom_profile=62.55 mm; D1=159.5 mm; DN=250.2 mm; FOD=197.5 mm; Fillet_Length=10 mm  [stored 0.0328084 ft]; Flange_thickness=22 mm  [stored 0.0721785 ft]; H3=720 mm; ID=125.1 mm; L=730 mm; L1=747 mm; L_Ref=738.5 mm; L_ref_2=325.62 mm; PG_Dia=80 mm; PG_Ref=121.67 mm; PG_depth=14 mm  [stored 0.0459318 ft]; PG_ref=135.1 mm; Pilot_Dia_1=47 mm; Pilot_Dia_1_Ref=56.4 mm; Pilot_Dia_1_Ref_2=112.8 mm; Pilot_Dia_2=79.9 mm; Pilot_Dia_3=31.33 mm; Pilot_Dia_4=15.67 mm; Pilot_Dia_5=10.44 mm; Pilot_top_1=456.13 mm; Pilot_top_ref=66.38 mm; Profile1_Height=335 mm; Profile1_Length=68.1 mm; Profile1_Length_2=45.4 mm; Profile_Dia=10 mm  [stored 0.0328084 ft]; Profile_Dia_2=10 mm  [stored 0.0328084 ft]; Profile_Dia_3=20 mm  [stored 0.0656168 ft]; Top_Profile=257.65 mm; Top_Profile_Ref=262.65 mm; Top_Ref=389.75 mm; Top_Ref_2=422.94 mm; W=510 mm; W_Ref=430.1 mm
- 879-0250-00-044002172A0_DN250_PN10: A=237.6 mm; Body_Collar_Dia=76.04 mm; Body_Collar_Dia_2=36.5 mm; Body_Flange_Dia=192.11 mm; Body_Flange_Dia_2=197.3 mm; Body_Height_1=182.5 mm; Body_Height_2=91.25 mm; Body_Height_3=81 mm; Body_Height_4=106.25 mm; Body_Top_Dia=22.81 mm; Body_Top_Dia_2=19.01 mm; Body_With_Dia=162.22 mm; Body_With_Dia_2=162.22 mm; Bolt_support=429.41 mm; Bolt_support_2=214.71 mm; Bolt_support_Dia=20 mm  [stored 0.0656168 ft]; Bolt_support_lenght=145.15 mm; Bolt_support_lenght_2=155.15 mm; Bottom_profile=62.58 mm; D1=159.5 mm; DN=250.3 mm; FOD=197.5 mm; Fillet_Length=10 mm  [stored 0.0328084 ft]; Flange_thickness=22 mm  [stored 0.0721785 ft]; H3=806 mm; ID=125.15 mm; L=730 mm; L1=747 mm; L_Ref=738.5 mm; L_ref_2=325.62 mm; PG_Dia=80 mm; PG_Ref=121.67 mm; PG_depth=14 mm  [stored 0.0459318 ft]; PG_ref=135.15 mm; Pilot_Dia_1=47 mm; Pilot_Dia_1_Ref=56.4 mm; Pilot_Dia_1_Ref_2=112.8 mm; Pilot_Dia_2=79.9 mm; Pilot_Dia_3=31.33 mm; Pilot_Dia_4=15.67 mm; Pilot_Dia_5=10.44 mm; Pilot_top_1=499.13 mm; Pilot_top_ref=109.38 mm; Profile1_Height=350 mm; Profile1_Length=68.1 mm; Profile1_Length_2=45.4 mm; Profile_Dia=10 mm  [stored 0.0328084 ft]; Profile_Dia_2=10 mm  [stored 0.0328084 ft]; Profile_Dia_3=20 mm  [stored 0.0656168 ft]; Top_Profile=257.65 mm; Top_Profile_Ref=262.65 mm; Top_Ref=389.75 mm; Top_Ref_2=444.44 mm; W=510 mm; W_Ref=430.1 mm
- 879-0250-00-04400227299_DN250_PN10: A=239.3 mm; Body_Collar_Dia=76.04 mm; Body_Collar_Dia_2=36.5 mm; Body_Flange_Dia=192.11 mm; Body_Flange_Dia_2=197.3 mm; Body_Height_1=182.5 mm; Body_Height_2=91.25 mm; Body_Height_3=81 mm; Body_Height_4=106.25 mm; Body_Top_Dia=22.81 mm; Body_Top_Dia_2=19.01 mm; Body_With_Dia=162.22 mm; Body_With_Dia_2=162.22 mm; Bolt_support=429.41 mm; Bolt_support_2=214.71 mm; Bolt_support_Dia=20 mm  [stored 0.0656168 ft]; Bolt_support_lenght=145.2 mm; Bolt_support_lenght_2=155.2 mm; Bottom_profile=62.6 mm; D1=159.5 mm; DN=250.4 mm; FOD=197.5 mm; Fillet_Length=10 mm  [stored 0.0328084 ft]; Flange_thickness=22 mm  [stored 0.0721785 ft]; H3=720 mm; ID=125.2 mm; L=730 mm; L1=747 mm; L_Ref=738.5 mm; L_ref_2=325.62 mm; PG_Dia=80 mm; PG_Ref=121.67 mm; PG_depth=14 mm  [stored 0.0459318 ft]; PG_ref=135.2 mm; Pilot_Dia_1=46 mm; Pilot_Dia_1_Ref=55.2 mm; Pilot_Dia_1_Ref_2=110.4 mm; Pilot_Dia_2=78.2 mm; Pilot_Dia_3=30.67 mm; Pilot_Dia_4=15.33 mm; Pilot_Dia_5=10.22 mm; Pilot_top_1=456.13 mm; Pilot_top_ref=66.38 mm; Profile1_Height=327 mm; Profile1_Length=68.1 mm; Profile1_Length_2=45.4 mm; Profile_Dia=10 mm  [stored 0.0328084 ft]; Profile_Dia_2=10 mm  [stored 0.0328084 ft]; Profile_Dia_3=20 mm  [stored 0.0656168 ft]; Top_Profile=257.65 mm; Top_Profile_Ref=262.65 mm; Top_Ref=389.75 mm; Top_Ref_2=422.94 mm; W=510 mm; W_Ref=431.8 mm
- 879-0250-00-044002272A0_DN250_PN10: A=239.3 mm; Body_Collar_Dia=76.04 mm; Body_Collar_Dia_2=36.5 mm; Body_Flange_Dia=192.11 mm; Body_Flange_Dia_2=197.3 mm; Body_Height_1=182.5 mm; Body_Height_2=91.25 mm; Body_Height_3=104.5 mm; Body_Height_4=106.25 mm; Body_Top_Dia=22.81 mm; Body_Top_Dia_2=19.01 mm; Body_With_Dia=162.22 mm; Body_With_Dia_2=162.22 mm; Bolt_support=429.41 mm; Bolt_support_2=214.71 mm; Bolt_support_Dia=20 mm  [stored 0.0656168 ft]; Bolt_support_lenght=145.25 mm; Bolt_support_lenght_2=155.25 mm; Bottom_profile=62.63 mm; D1=159.5 mm; DN=250.5 mm; FOD=197.5 mm; Fillet_Length=10 mm  [stored 0.0328084 ft]; Flange_thickness=22 mm  [stored 0.0721785 ft]; H3=806 mm; ID=125.25 mm; L=730 mm; L1=747 mm; L_Ref=738.5 mm; L_ref_2=325.62 mm; PG_Dia=80 mm; PG_Ref=121.67 mm; PG_depth=14 mm  [stored 0.0459318 ft]; PG_ref=135.25 mm; Pilot_Dia_1=46 mm; Pilot_Dia_1_Ref=55.2 mm; Pilot_Dia_1_Ref_2=110.4 mm; Pilot_Dia_2=78.2 mm; Pilot_Dia_3=30.67 mm; Pilot_Dia_4=15.33 mm; Pilot_Dia_5=10.22 mm; Pilot_top_1=510.88 mm; Pilot_top_ref=97.63 mm; Profile1_Height=330 mm; Profile1_Length=68.1 mm; Profile1_Length_2=45.4 mm; Profile_Dia=10 mm  [stored 0.0328084 ft]; Profile_Dia_2=10 mm  [stored 0.0328084 ft]; Profile_Dia_3=20 mm  [stored 0.0656168 ft]; Top_Profile=257.65 mm; Top_Profile_Ref=262.65 mm; Top_Ref=413.25 mm; Top_Ref_2=462.06 mm; W=510 mm; W_Ref=431.8 mm
- 879-0250-00-04400237299_DN250_PN10: A=237.6 mm; Body_Collar_Dia=76.04 mm; Body_Collar_Dia_2=36.5 mm; Body_Flange_Dia=192.11 mm; Body_Flange_Dia_2=197.3 mm; Body_Height_1=182.5 mm; Body_Height_2=91.25 mm; Body_Height_3=81 mm; Body_Height_4=106.25 mm; Body_Top_Dia=22.81 mm; Body_Top_Dia_2=19.01 mm; Body_With_Dia=162.22 mm; Body_With_Dia_2=162.22 mm; Bolt_support=429.41 mm; Bolt_support_2=214.71 mm; Bolt_support_Dia=20 mm  [stored 0.0656168 ft]; Bolt_support_lenght=145.3 mm; Bolt_support_lenght_2=155.3 mm; Bottom_profile=62.65 mm; D1=159.5 mm; DN=250.6 mm; FOD=197.5 mm; Fillet_Length=10 mm  [stored 0.0328084 ft]; Flange_thickness=22 mm  [stored 0.0721785 ft]; H3=720 mm; ID=125.3 mm; L=730 mm; L1=747 mm; L_Ref=738.5 mm; L_ref_2=325.62 mm; PG_Dia=80 mm; PG_Ref=121.67 mm; PG_depth=14 mm  [stored 0.0459318 ft]; PG_ref=135.3 mm; Pilot_Dia_1=47 mm; Pilot_Dia_1_Ref=56.4 mm; Pilot_Dia_1_Ref_2=112.8 mm; Pilot_Dia_2=79.9 mm; Pilot_Dia_3=31.33 mm; Pilot_Dia_4=15.67 mm; Pilot_Dia_5=10.44 mm; Pilot_top_1=456.13 mm; Pilot_top_ref=66.38 mm; Profile1_Height=335 mm; Profile1_Length=68.1 mm; Profile1_Length_2=45.4 mm; Profile_Dia=10 mm  [stored 0.0328084 ft]; Profile_Dia_2=10 mm  [stored 0.0328084 ft]; Profile_Dia_3=20 mm  [stored 0.0656168 ft]; Top_Profile=257.65 mm; Top_Profile_Ref=262.65 mm; Top_Ref=389.75 mm; Top_Ref_2=422.94 mm; W=510 mm; W_Ref=430.1 mm
- 879-0250-00-14400207299_DN250_PN16: A=234.3 mm; Body_Collar_Dia=76.04 mm; Body_Collar_Dia_2=36.5 mm; Body_Flange_Dia=192.11 mm; Body_Flange_Dia_2=197.3 mm; Body_Height_1=182.5 mm; Body_Height_2=91.25 mm; Body_Height_3=81 mm; Body_Height_4=106.25 mm; Body_Top_Dia=22.81 mm; Body_Top_Dia_2=19.01 mm; Body_With_Dia=162.22 mm; Body_With_Dia_2=162.22 mm; Bolt_support=429.41 mm; Bolt_support_2=214.71 mm; Bolt_support_Dia=20 mm  [stored 0.0656168 ft]; Bolt_support_lenght=145.4 mm; Bolt_support_lenght_2=155.4 mm; Bottom_profile=62.7 mm; D1=159.5 mm; DN=250.8 mm; FOD=202.5 mm; Fillet_Length=10 mm  [stored 0.0328084 ft]; Flange_thickness=22 mm  [stored 0.0721785 ft]; H3=720 mm; ID=125.4 mm; L=730 mm; L1=747 mm; L_Ref=738.5 mm; L_ref_2=325.62 mm; PG_Dia=80 mm; PG_Ref=121.67 mm; PG_depth=14 mm  [stored 0.0459318 ft]; PG_ref=135.4 mm; Pilot_Dia_1=46 mm; Pilot_Dia_1_Ref=55.2 mm; Pilot_Dia_1_Ref_2=110.4 mm; Pilot_Dia_2=78.2 mm; Pilot_Dia_3=30.67 mm; Pilot_Dia_4=15.33 mm; Pilot_Dia_5=10.22 mm; Pilot_top_1=453.63 mm; Pilot_top_ref=63.88 mm; Profile1_Height=327 mm; Profile1_Length=69.83 mm; Profile1_Length_2=46.55 mm; Profile_Dia=10 mm  [stored 0.0328084 ft]; Profile_Dia_2=10 mm  [stored 0.0328084 ft]; Profile_Dia_3=20 mm  [stored 0.0656168 ft]; Top_Profile=257.65 mm; Top_Profile_Ref=262.65 mm; Top_Ref=389.75 mm; Top_Ref_2=421.69 mm; W=510 mm; W_Ref=431.8 mm
- 879-0250-00-144002072A0_DN250_PN16: A=234.3 mm; Body_Collar_Dia=76.04 mm; Body_Collar_Dia_2=36.5 mm; Body_Flange_Dia=192.11 mm; Body_Flange_Dia_2=197.3 mm; Body_Height_1=182.5 mm; Body_Height_2=91.25 mm; Body_Height_3=104.5 mm; Body_Height_4=106.25 mm; Body_Top_Dia=22.81 mm; Body_Top_Dia_2=19.01 mm; Body_With_Dia=162.22 mm; Body_With_Dia_2=162.22 mm; Bolt_support=429.41 mm; Bolt_support_2=214.71 mm; Bolt_support_Dia=20 mm  [stored 0.0656168 ft]; Bolt_support_lenght=145.45 mm; Bolt_support_lenght_2=155.45 mm; Bottom_profile=62.73 mm; D1=159.5 mm; DN=250.9 mm; FOD=202.5 mm; Fillet_Length=10 mm  [stored 0.0328084 ft]; Flange_thickness=22 mm  [stored 0.0721785 ft]; H3=806 mm; ID=125.45 mm; L=730 mm; L1=747 mm; L_Ref=738.5 mm; L_ref_2=325.62 mm; PG_Dia=80 mm; PG_Ref=121.67 mm; PG_depth=14 mm  [stored 0.0459318 ft]; PG_ref=135.45 mm; Pilot_Dia_1=46 mm; Pilot_Dia_1_Ref=55.2 mm; Pilot_Dia_1_Ref_2=110.4 mm; Pilot_Dia_2=78.2 mm; Pilot_Dia_3=30.67 mm; Pilot_Dia_4=15.33 mm; Pilot_Dia_5=10.22 mm; Pilot_top_1=508.38 mm; Pilot_top_ref=95.13 mm; Profile1_Height=330 mm; Profile1_Length=69.83 mm; Profile1_Length_2=46.55 mm; Profile_Dia=10 mm  [stored 0.0328084 ft]; Profile_Dia_2=10 mm  [stored 0.0328084 ft]; Profile_Dia_3=20 mm  [stored 0.0656168 ft]; Top_Profile=257.65 mm; Top_Profile_Ref=262.65 mm; Top_Ref=413.25 mm; Top_Ref_2=460.81 mm; W=510 mm; W_Ref=431.8 mm
- 879-0250-00-14400217299_DN250_PN16: A=232.6 mm; Body_Collar_Dia=76.04 mm; Body_Collar_Dia_2=36.5 mm; Body_Flange_Dia=192.11 mm; Body_Flange_Dia_2=197.3 mm; Body_Height_1=182.5 mm; Body_Height_2=91.25 mm; Body_Height_3=81 mm; Body_Height_4=106.25 mm; Body_Top_Dia=22.81 mm; Body_Top_Dia_2=19.01 mm; Body_With_Dia=162.22 mm; Body_With_Dia_2=162.22 mm; Bolt_support=429.41 mm; Bolt_support_2=214.71 mm; Bolt_support_Dia=20 mm  [stored 0.0656168 ft]; Bolt_support_lenght=145.06 mm; Bolt_support_lenght_2=155.06 mm; Bottom_profile=62.53 mm; D1=159.5 mm; DN=250.11 mm; FOD=202.5 mm; Fillet_Length=10 mm  [stored 0.0328084 ft]; Flange_thickness=22 mm  [stored 0.0721785 ft]; H3=720 mm; ID=125.06 mm; L=730 mm; L1=747 mm; L_Ref=738.5 mm; L_ref_2=325.62 mm; PG_Dia=80 mm; PG_Ref=121.67 mm; PG_depth=14 mm  [stored 0.0459318 ft]; PG_ref=135.06 mm; Pilot_Dia_1=47 mm; Pilot_Dia_1_Ref=56.4 mm; Pilot_Dia_1_Ref_2=112.8 mm; Pilot_Dia_2=79.9 mm; Pilot_Dia_3=31.33 mm; Pilot_Dia_4=15.67 mm; Pilot_Dia_5=10.44 mm; Pilot_top_1=453.63 mm; Pilot_top_ref=63.88 mm; Profile1_Height=335 mm; Profile1_Length=69.83 mm; Profile1_Length_2=46.55 mm; Profile_Dia=10 mm  [stored 0.0328084 ft]; Profile_Dia_2=10 mm  [stored 0.0328084 ft]; Profile_Dia_3=20 mm  [stored 0.0656168 ft]; Top_Profile=257.65 mm; Top_Profile_Ref=262.65 mm; Top_Ref=389.75 mm; Top_Ref_2=421.69 mm; W=510 mm; W_Ref=430.1 mm
- 879-0250-00-144002172A0_DN250_PN16: A=232.6 mm; Body_Collar_Dia=76.04 mm; Body_Collar_Dia_2=36.5 mm; Body_Flange_Dia=192.11 mm; Body_Flange_Dia_2=197.3 mm; Body_Height_1=182.5 mm; Body_Height_2=91.25 mm; Body_Height_3=81 mm; Body_Height_4=106.25 mm; Body_Top_Dia=22.81 mm; Body_Top_Dia_2=19.01 mm; Body_With_Dia=162.22 mm; Body_With_Dia_2=162.22 mm; Bolt_support=429.41 mm; Bolt_support_2=214.71 mm; Bolt_support_Dia=20 mm  [stored 0.0656168 ft]; Bolt_support_lenght=145.06 mm; Bolt_support_lenght_2=155.06 mm; Bottom_profile=62.53 mm; D1=159.5 mm; DN=250.12 mm; FOD=202.5 mm; Fillet_Length=10 mm  [stored 0.0328084 ft]; Flange_thickness=22 mm  [stored 0.0721785 ft]; H3=806 mm; ID=125.06 mm; L=730 mm; L1=747 mm; L_Ref=738.5 mm; L_ref_2=325.62 mm; PG_Dia=80 mm; PG_Ref=121.67 mm; PG_depth=14 mm  [stored 0.0459318 ft]; PG_ref=135.06 mm; Pilot_Dia_1=47 mm; Pilot_Dia_1_Ref=56.4 mm; Pilot_Dia_1_Ref_2=112.8 mm; Pilot_Dia_2=79.9 mm; Pilot_Dia_3=31.33 mm; Pilot_Dia_4=15.67 mm; Pilot_Dia_5=10.44 mm; Pilot_top_1=496.63 mm; Pilot_top_ref=106.88 mm; Profile1_Height=350 mm; Profile1_Length=69.83 mm; Profile1_Length_2=46.55 mm; Profile_Dia=10 mm  [stored 0.0328084 ft]; Profile_Dia_2=10 mm  [stored 0.0328084 ft]; Profile_Dia_3=20 mm  [stored 0.0656168 ft]; Top_Profile=257.65 mm; Top_Profile_Ref=262.65 mm; Top_Ref=389.75 mm; Top_Ref_2=443.19 mm; W=510 mm; W_Ref=430.1 mm
- 879-0250-00-14400227299_DN250_PN16: A=234.3 mm; Body_Collar_Dia=76.04 mm; Body_Collar_Dia_2=36.5 mm; Body_Flange_Dia=192.11 mm; Body_Flange_Dia_2=197.3 mm; Body_Height_1=182.5 mm; Body_Height_2=91.25 mm; Body_Height_3=81 mm; Body_Height_4=106.25 mm; Body_Top_Dia=22.81 mm; Body_Top_Dia_2=19.01 mm; Body_With_Dia=162.22 mm; Body_With_Dia_2=162.22 mm; Bolt_support=429.41 mm; Bolt_support_2=214.71 mm; Bolt_support_Dia=20 mm  [stored 0.0656168 ft]; Bolt_support_lenght=145.07 mm; Bolt_support_lenght_2=155.07 mm; Bottom_profile=62.53 mm; D1=159.5 mm; DN=250.13 mm; FOD=202.5 mm; Fillet_Length=10 mm  [stored 0.0328084 ft]; Flange_thickness=22 mm  [stored 0.0721785 ft]; H3=720 mm; ID=125.07 mm; L=730 mm; L1=747 mm; L_Ref=738.5 mm; L_ref_2=325.62 mm; PG_Dia=80 mm; PG_Ref=121.67 mm; PG_depth=14 mm  [stored 0.0459318 ft]; PG_ref=135.07 mm; Pilot_Dia_1=46 mm; Pilot_Dia_1_Ref=55.2 mm; Pilot_Dia_1_Ref_2=110.4 mm; Pilot_Dia_2=78.2 mm; Pilot_Dia_3=30.67 mm; Pilot_Dia_4=15.33 mm; Pilot_Dia_5=10.22 mm; Pilot_top_1=453.63 mm; Pilot_top_ref=63.88 mm; Profile1_Height=327 mm; Profile1_Length=69.83 mm; Profile1_Length_2=46.55 mm; Profile_Dia=10 mm  [stored 0.0328084 ft]; Profile_Dia_2=10 mm  [stored 0.0328084 ft]; Profile_Dia_3=20 mm  [stored 0.0656168 ft]; Top_Profile=257.65 mm; Top_Profile_Ref=262.65 mm; Top_Ref=389.75 mm; Top_Ref_2=421.69 mm; W=510 mm; W_Ref=431.8 mm
- 879-0250-00-144002272A0_DN250_PN16: A=234.3 mm; Body_Collar_Dia=76.04 mm; Body_Collar_Dia_2=36.5 mm; Body_Flange_Dia=192.11 mm; Body_Flange_Dia_2=197.3 mm; Body_Height_1=182.5 mm; Body_Height_2=91.25 mm; Body_Height_3=104.5 mm; Body_Height_4=106.25 mm; Body_Top_Dia=22.81 mm; Body_Top_Dia_2=19.01 mm; Body_With_Dia=162.22 mm; Body_With_Dia_2=162.22 mm; Bolt_support=429.41 mm; Bolt_support_2=214.71 mm; Bolt_support_Dia=20 mm  [stored 0.0656168 ft]; Bolt_support_lenght=145.07 mm; Bolt_support_lenght_2=155.07 mm; Bottom_profile=62.54 mm; D1=159.5 mm; DN=250.14 mm; FOD=202.5 mm; Fillet_Length=10 mm  [stored 0.0328084 ft]; Flange_thickness=22 mm  [stored 0.0721785 ft]; H3=806 mm; ID=125.07 mm; L=730 mm; L1=747 mm; L_Ref=738.5 mm; L_ref_2=325.62 mm; PG_Dia=80 mm; PG_Ref=121.67 mm; PG_depth=14 mm  [stored 0.0459318 ft]; PG_ref=135.07 mm; Pilot_Dia_1=46 mm; Pilot_Dia_1_Ref=55.2 mm; Pilot_Dia_1_Ref_2=110.4 mm; Pilot_Dia_2=78.2 mm; Pilot_Dia_3=30.67 mm; Pilot_Dia_4=15.33 mm; Pilot_Dia_5=10.22 mm; Pilot_top_1=508.38 mm; Pilot_top_ref=95.13 mm; Profile1_Height=330 mm; Profile1_Length=69.83 mm; Profile1_Length_2=46.55 mm; Profile_Dia=10 mm  [stored 0.0328084 ft]; Profile_Dia_2=10 mm  [stored 0.0328084 ft]; Profile_Dia_3=20 mm  [stored 0.0656168 ft]; Top_Profile=257.65 mm; Top_Profile_Ref=262.65 mm; Top_Ref=413.25 mm; Top_Ref_2=460.81 mm; W=510 mm; W_Ref=431.8 mm
- 879-0250-00-14400237299_DN250_PN16: A=232.6 mm; Body_Collar_Dia=76.04 mm; Body_Collar_Dia_2=36.5 mm; Body_Flange_Dia=192.11 mm; Body_Flange_Dia_2=197.3 mm; Body_Height_1=182.5 mm; Body_Height_2=91.25 mm; Body_Height_3=81 mm; Body_Height_4=106.25 mm; Body_Top_Dia=22.81 mm; Body_Top_Dia_2=19.01 mm; Body_With_Dia=162.22 mm; Body_With_Dia_2=162.22 mm; Bolt_support=429.41 mm; Bolt_support_2=214.71 mm; Bolt_support_Dia=20 mm  [stored 0.0656168 ft]; Bolt_support_lenght=145.08 mm; Bolt_support_lenght_2=155.08 mm; Bottom_profile=62.54 mm; D1=159.5 mm; DN=250.15 mm; FOD=202.5 mm; Fillet_Length=10 mm  [stored 0.0328084 ft]; Flange_thickness=22 mm  [stored 0.0721785 ft]; H3=720 mm; ID=125.08 mm; L=730 mm; L1=747 mm; L_Ref=738.5 mm; L_ref_2=325.62 mm; PG_Dia=80 mm; PG_Ref=121.67 mm; PG_depth=14 mm  [stored 0.0459318 ft]; PG_ref=135.08 mm; Pilot_Dia_1=47 mm; Pilot_Dia_1_Ref=56.4 mm; Pilot_Dia_1_Ref_2=112.8 mm; Pilot_Dia_2=79.9 mm; Pilot_Dia_3=31.33 mm; Pilot_Dia_4=15.67 mm; Pilot_Dia_5=10.44 mm; Pilot_top_1=453.63 mm; Pilot_top_ref=63.88 mm; Profile1_Height=335 mm; Profile1_Length=69.83 mm; Profile1_Length_2=46.55 mm; Profile_Dia=10 mm  [stored 0.0328084 ft]; Profile_Dia_2=10 mm  [stored 0.0328084 ft]; Profile_Dia_3=20 mm  [stored 0.0656168 ft]; Top_Profile=257.65 mm; Top_Profile_Ref=262.65 mm; Top_Ref=389.75 mm; Top_Ref_2=421.69 mm; W=510 mm; W_Ref=430.1 mm
- 879-0250-00-144002372A0_DN250_PN16: A=232.6 mm; Body_Collar_Dia=76.04 mm; Body_Collar_Dia_2=36.5 mm; Body_Flange_Dia=192.11 mm; Body_Flange_Dia_2=197.3 mm; Body_Height_1=182.5 mm; Body_Height_2=91.25 mm; Body_Height_3=81 mm; Body_Height_4=106.25 mm; Body_Top_Dia=22.81 mm; Body_Top_Dia_2=19.01 mm; Body_With_Dia=162.22 mm; Body_With_Dia_2=162.22 mm; Bolt_support=429.41 mm; Bolt_support_2=214.71 mm; Bolt_support_Dia=20 mm  [stored 0.0656168 ft]; Bolt_support_lenght=145.08 mm; Bolt_support_lenght_2=155.08 mm; Bottom_profile=62.54 mm; D1=159.5 mm; DN=250.16 mm; FOD=202.5 mm; Fillet_Length=10 mm  [stored 0.0328084 ft]; Flange_thickness=22 mm  [stored 0.0721785 ft]; H3=806 mm; ID=125.08 mm; L=730 mm; L1=747 mm; L_Ref=738.5 mm; L_ref_2=325.62 mm; PG_Dia=80 mm; PG_Ref=121.67 mm; PG_depth=14 mm  [stored 0.0459318 ft]; PG_ref=135.08 mm; Pilot_Dia_1=47 mm; Pilot_Dia_1_Ref=56.4 mm; Pilot_Dia_1_Ref_2=112.8 mm; Pilot_Dia_2=79.9 mm; Pilot_Dia_3=31.33 mm; Pilot_Dia_4=15.67 mm; Pilot_Dia_5=10.44 mm; Pilot_top_1=496.63 mm; Pilot_top_ref=106.88 mm; Profile1_Height=350 mm; Profile1_Length=69.83 mm; Profile1_Length_2=46.55 mm; Profile_Dia=10 mm  [stored 0.0328084 ft]; Profile_Dia_2=10 mm  [stored 0.0328084 ft]; Profile_Dia_3=20 mm  [stored 0.0656168 ft]; Top_Profile=257.65 mm; Top_Profile_Ref=262.65 mm; Top_Ref=389.75 mm; Top_Ref_2=443.19 mm; W=510 mm; W_Ref=430.1 mm
- 879-0300-00-04400207299_DN300_PN10: A=248.25 mm; Body_Collar_Dia=88.54 mm; Body_Collar_Dia_2=42.5 mm; Body_Flange_Dia=223.68 mm; Body_Flange_Dia_2=229.73 mm; Body_Height_1=212.5 mm; Body_Height_2=106.25 mm; Body_Height_3=94.5 mm; Body_Height_4=121.25 mm; Body_Top_Dia=26.56 mm; Body_Top_Dia_2=22.14 mm; Body_With_Dia=188.89 mm; Body_With_Dia_2=188.89 mm; Bolt_support=500 mm; Bolt_support_2=250 mm; Bolt_support_Dia=20 mm  [stored 0.0656168 ft]; Bolt_support_lenght=170 mm; Bolt_support_lenght_2=180 mm; Bottom_profile=75 mm; D1=185 mm; DN=300 mm; FOD=222.5 mm; Fillet_Length=10 mm  [stored 0.0328084 ft]; Flange_thickness=24.5 mm  [stored 0.0803806 ft]; H3=790 mm; ID=150 mm; L=850 mm; L1=867 mm; L_Ref=858.5 mm; L_ref_2=380.26 mm; PG_Dia=90 mm; PG_Ref=141.67 mm; PG_depth=14 mm  [stored 0.0459318 ft]; PG_ref=160 mm; Pilot_Dia_1=52.5 mm; Pilot_Dia_1_Ref=63 mm; Pilot_Dia_1_Ref_2=126 mm; Pilot_Dia_2=89.25 mm; Pilot_Dia_3=35 mm  [stored 0.114829 ft]; Pilot_Dia_4=17.5 mm  [stored 0.0574147 ft]; Pilot_Dia_5=11.67 mm; Pilot_top_1=507.88 mm; Pilot_top_ref=59.63 mm; Profile1_Height=361 mm; Profile1_Length=76.72 mm; Profile1_Length_2=51.15 mm; Profile_Dia=10 mm  [stored 0.0328084 ft]; Profile_Dia_2=10 mm  [stored 0.0328084 ft]; Profile_Dia_3=20 mm  [stored 0.0656168 ft]; Top_Profile=300 mm; Top_Profile_Ref=305 mm; Top_Ref=448.25 mm; Top_Ref_2=478.06 mm; W=555 mm; W_Ref=465.75 mm
- 879-0300-00-044002072A0_DN300_PN10: A=248.25 mm; Body_Collar_Dia=88.54 mm; Body_Collar_Dia_2=42.5 mm; Body_Flange_Dia=223.68 mm; Body_Flange_Dia_2=229.73 mm; Body_Height_1=212.5 mm; Body_Height_2=106.25 mm; Body_Height_3=106 mm; Body_Height_4=121.25 mm; Body_Top_Dia=26.56 mm; Body_Top_Dia_2=22.14 mm; Body_With_Dia=188.89 mm; Body_With_Dia_2=188.89 mm; Bolt_support=500 mm; Bolt_support_2=250 mm; Bolt_support_Dia=20 mm  [stored 0.0656168 ft]; Bolt_support_lenght=170.05 mm; Bolt_support_lenght_2=180.05 mm; Bottom_profile=75.03 mm; D1=185 mm; DN=300.1 mm; FOD=222.5 mm; Fillet_Length=10 mm  [stored 0.0328084 ft]; Flange_thickness=24.5 mm  [stored 0.0803806 ft]; H3=881 mm; ID=150.05 mm; L=850 mm; L1=867 mm; L_Ref=858.5 mm; L_ref_2=380.26 mm; PG_Dia=90 mm; PG_Ref=141.67 mm; PG_depth=14 mm  [stored 0.0459318 ft]; PG_ref=160.05 mm; Pilot_Dia_1=52.5 mm; Pilot_Dia_1_Ref=63 mm; Pilot_Dia_1_Ref_2=126 mm; Pilot_Dia_2=89.25 mm; Pilot_Dia_3=35 mm  [stored 0.114829 ft]; Pilot_Dia_4=17.5 mm  [stored 0.0574147 ft]; Pilot_Dia_5=11.67 mm; Pilot_top_1=559.13 mm; Pilot_top_ref=99.38 mm; Profile1_Height=400 mm; Profile1_Length=76.72 mm; Profile1_Length_2=51.15 mm; Profile_Dia=10 mm  [stored 0.0328084 ft]; Profile_Dia_2=10 mm  [stored 0.0328084 ft]; Profile_Dia_3=20 mm  [stored 0.0656168 ft]; Top_Profile=300 mm; Top_Profile_Ref=305 mm; Top_Ref=459.75 mm; Top_Ref_2=509.44 mm; W=555 mm; W_Ref=465.75 mm
- 879-0300-00-04400217299_DN300_PN10: A=244.85 mm; Body_Collar_Dia=88.54 mm; Body_Collar_Dia_2=42.5 mm; Body_Flange_Dia=223.68 mm; Body_Flange_Dia_2=229.73 mm; Body_Height_1=212.5 mm; Body_Height_2=106.25 mm; Body_Height_3=94.5 mm; Body_Height_4=121.25 mm; Body_Top_Dia=26.56 mm; Body_Top_Dia_2=22.14 mm; Body_With_Dia=188.89 mm; Body_With_Dia_2=188.89 mm; Bolt_support=500 mm; Bolt_support_2=250 mm; Bolt_support_Dia=20 mm  [stored 0.0656168 ft]; Bolt_support_lenght=170.1 mm; Bolt_support_lenght_2=180.1 mm; Bottom_profile=75.05 mm; D1=185 mm; DN=300.2 mm; FOD=222.5 mm; Fillet_Length=10 mm  [stored 0.0328084 ft]; Flange_thickness=24.5 mm  [stored 0.0803806 ft]; H3=790 mm; ID=150.1 mm; L=850 mm; L1=867 mm; L_Ref=858.5 mm; L_ref_2=380.26 mm; PG_Dia=90 mm; PG_Ref=141.67 mm; PG_depth=14 mm  [stored 0.0459318 ft]; PG_ref=160.1 mm; Pilot_Dia_1=54.5 mm; Pilot_Dia_1_Ref=65.4 mm; Pilot_Dia_1_Ref_2=130.8 mm; Pilot_Dia_2=92.65 mm; Pilot_Dia_3=36.33 mm; Pilot_Dia_4=18.17 mm; Pilot_Dia_5=12.11 mm; Pilot_top_1=507.88 mm; Pilot_top_ref=59.63 mm; Profile1_Height=380 mm; Profile1_Length=76.72 mm; Profile1_Length_2=51.15 mm; Profile_Dia=10 mm  [stored 0.0328084 ft]; Profile_Dia_2=10 mm  [stored 0.0328084 ft]; Profile_Dia_3=20 mm  [stored 0.0656168 ft]; Top_Profile=300 mm; Top_Profile_Ref=305 mm; Top_Ref=448.25 mm; Top_Ref_2=478.06 mm; W=555 mm; W_Ref=462.35 mm
- 879-0300-00-044002172A0_DN300_PN10: A=244.85 mm; Body_Collar_Dia=88.54 mm; Body_Collar_Dia_2=42.5 mm; Body_Flange_Dia=223.68 mm; Body_Flange_Dia_2=229.73 mm; Body_Height_1=212.5 mm; Body_Height_2=106.25 mm; Body_Height_3=94.5 mm; Body_Height_4=121.25 mm; Body_Top_Dia=26.56 mm; Body_Top_Dia_2=22.14 mm; Body_With_Dia=188.89 mm; Body_With_Dia_2=188.89 mm; Bolt_support=500 mm; Bolt_support_2=250 mm; Bolt_support_Dia=20 mm  [stored 0.0656168 ft]; Bolt_support_lenght=170.15 mm; Bolt_support_lenght_2=180.15 mm; Bottom_profile=75.08 mm; D1=185 mm; DN=300.3 mm; FOD=222.5 mm; Fillet_Length=10 mm  [stored 0.0328084 ft]; Flange_thickness=24.5 mm  [stored 0.0803806 ft]; H3=881 mm; ID=150.15 mm; L=850 mm; L1=867 mm; L_Ref=858.5 mm; L_ref_2=380.26 mm; PG_Dia=90 mm; PG_Ref=141.67 mm; PG_depth=14 mm  [stored 0.0459318 ft]; PG_ref=160.15 mm; Pilot_Dia_1=54.5 mm; Pilot_Dia_1_Ref=65.4 mm; Pilot_Dia_1_Ref_2=130.8 mm; Pilot_Dia_2=92.65 mm; Pilot_Dia_3=36.33 mm; Pilot_Dia_4=18.17 mm; Pilot_Dia_5=12.11 mm; Pilot_top_1=553.38 mm; Pilot_top_ref=105.13 mm; Profile1_Height=380 mm; Profile1_Length=76.72 mm; Profile1_Length_2=51.15 mm; Profile_Dia=10 mm  [stored 0.0328084 ft]; Profile_Dia_2=10 mm  [stored 0.0328084 ft]; Profile_Dia_3=20 mm  [stored 0.0656168 ft]; Top_Profile=300 mm; Top_Profile_Ref=305 mm; Top_Ref=448.25 mm; Top_Ref_2=500.81 mm; W=555 mm; W_Ref=462.35 mm
- 879-0300-00-04400227299_DN300_PN10: A=248.25 mm; Body_Collar_Dia=88.54 mm; Body_Collar_Dia_2=42.5 mm; Body_Flange_Dia=223.68 mm; Body_Flange_Dia_2=229.73 mm; Body_Height_1=212.5 mm; Body_Height_2=106.25 mm; Body_Height_3=94.5 mm; Body_Height_4=121.25 mm; Body_Top_Dia=26.56 mm; Body_Top_Dia_2=22.14 mm; Body_With_Dia=188.89 mm; Body_With_Dia_2=188.89 mm; Bolt_support=500 mm; Bolt_support_2=250 mm; Bolt_support_Dia=20 mm  [stored 0.0656168 ft]; Bolt_support_lenght=170.2 mm; Bolt_support_lenght_2=180.2 mm; Bottom_profile=75.1 mm; D1=185 mm; DN=300.4 mm; FOD=222.5 mm; Fillet_Length=10 mm  [stored 0.0328084 ft]; Flange_thickness=24.5 mm  [stored 0.0803806 ft]; H3=790 mm; ID=150.2 mm; L=850 mm; L1=867 mm; L_Ref=858.5 mm; L_ref_2=380.26 mm; PG_Dia=90 mm; PG_Ref=141.67 mm; PG_depth=14 mm  [stored 0.0459318 ft]; PG_ref=160.2 mm; Pilot_Dia_1=52.5 mm; Pilot_Dia_1_Ref=63 mm; Pilot_Dia_1_Ref_2=126 mm; Pilot_Dia_2=89.25 mm; Pilot_Dia_3=35 mm  [stored 0.114829 ft]; Pilot_Dia_4=17.5 mm  [stored 0.0574147 ft]; Pilot_Dia_5=11.67 mm; Pilot_top_1=507.88 mm; Pilot_top_ref=59.63 mm; Profile1_Height=361 mm; Profile1_Length=76.72 mm; Profile1_Length_2=51.15 mm; Profile_Dia=10 mm  [stored 0.0328084 ft]; Profile_Dia_2=10 mm  [stored 0.0328084 ft]; Profile_Dia_3=20 mm  [stored 0.0656168 ft]; Top_Profile=300 mm; Top_Profile_Ref=305 mm; Top_Ref=448.25 mm; Top_Ref_2=478.06 mm; W=555 mm; W_Ref=465.75 mm
- 879-0300-00-044002272A0_DN300_PN10: A=248.25 mm; Body_Collar_Dia=88.54 mm; Body_Collar_Dia_2=42.5 mm; Body_Flange_Dia=223.68 mm; Body_Flange_Dia_2=229.73 mm; Body_Height_1=212.5 mm; Body_Height_2=106.25 mm; Body_Height_3=106 mm; Body_Height_4=121.25 mm; Body_Top_Dia=26.56 mm; Body_Top_Dia_2=22.14 mm; Body_With_Dia=188.89 mm; Body_With_Dia_2=188.89 mm; Bolt_support=500 mm; Bolt_support_2=250 mm; Bolt_support_Dia=20 mm  [stored 0.0656168 ft]; Bolt_support_lenght=170.25 mm; Bolt_support_lenght_2=180.25 mm; Bottom_profile=75.13 mm; D1=185 mm; DN=300.5 mm; FOD=222.5 mm; Fillet_Length=10 mm  [stored 0.0328084 ft]; Flange_thickness=24.5 mm  [stored 0.0803806 ft]; H3=881 mm; ID=150.25 mm; L=850 mm; L1=867 mm; L_Ref=858.5 mm; L_ref_2=380.26 mm; PG_Dia=90 mm; PG_Ref=141.67 mm; PG_depth=14 mm  [stored 0.0459318 ft]; PG_ref=160.25 mm; Pilot_Dia_1=52.5 mm; Pilot_Dia_1_Ref=63 mm; Pilot_Dia_1_Ref_2=126 mm; Pilot_Dia_2=89.25 mm; Pilot_Dia_3=35 mm  [stored 0.114829 ft]; Pilot_Dia_4=17.5 mm  [stored 0.0574147 ft]; Pilot_Dia_5=11.67 mm; Pilot_top_1=559.13 mm; Pilot_top_ref=99.38 mm; Profile1_Height=400 mm; Profile1_Length=76.72 mm; Profile1_Length_2=51.15 mm; Profile_Dia=10 mm  [stored 0.0328084 ft]; Profile_Dia_2=10 mm  [stored 0.0328084 ft]; Profile_Dia_3=20 mm  [stored 0.0656168 ft]; Top_Profile=300 mm; Top_Profile_Ref=305 mm; Top_Ref=459.75 mm; Top_Ref_2=509.44 mm; W=555 mm; W_Ref=465.75 mm
- 879-0300-00-04400237290_DN300_PN10: A=244.85 mm; Body_Collar_Dia=88.54 mm; Body_Collar_Dia_2=42.5 mm; Body_Flange_Dia=223.68 mm; Body_Flange_Dia_2=229.73 mm; Body_Height_1=212.5 mm; Body_Height_2=106.25 mm; Body_Height_3=94.5 mm; Body_Height_4=121.25 mm; Body_Top_Dia=26.56 mm; Body_Top_Dia_2=22.14 mm; Body_With_Dia=188.89 mm; Body_With_Dia_2=188.89 mm; Bolt_support=500 mm; Bolt_support_2=250 mm; Bolt_support_Dia=20 mm  [stored 0.0656168 ft]; Bolt_support_lenght=170.3 mm; Bolt_support_lenght_2=180.3 mm; Bottom_profile=75.15 mm; D1=185 mm; DN=300.6 mm; FOD=222.5 mm; Fillet_Length=10 mm  [stored 0.0328084 ft]; Flange_thickness=24.5 mm  [stored 0.0803806 ft]; H3=790 mm; ID=150.3 mm; L=850 mm; L1=867 mm; L_Ref=858.5 mm; L_ref_2=380.26 mm; PG_Dia=90 mm; PG_Ref=141.67 mm; PG_depth=14 mm  [stored 0.0459318 ft]; PG_ref=160.3 mm; Pilot_Dia_1=54.5 mm; Pilot_Dia_1_Ref=65.4 mm; Pilot_Dia_1_Ref_2=130.8 mm; Pilot_Dia_2=92.65 mm; Pilot_Dia_3=36.33 mm; Pilot_Dia_4=18.17 mm; Pilot_Dia_5=12.11 mm; Pilot_top_1=507.88 mm; Pilot_top_ref=59.63 mm; Profile1_Height=380 mm; Profile1_Length=76.72 mm; Profile1_Length_2=51.15 mm; Profile_Dia=10 mm  [stored 0.0328084 ft]; Profile_Dia_2=10 mm  [stored 0.0328084 ft]; Profile_Dia_3=20 mm  [stored 0.0656168 ft]; Top_Profile=300 mm; Top_Profile_Ref=305 mm; Top_Ref=448.25 mm; Top_Ref_2=478.06 mm; W=555 mm; W_Ref=462.35 mm
- 879-0300-00-044002372A0_DN300_PN10: A=244.85 mm; Body_Collar_Dia=88.54 mm; Body_Collar_Dia_2=42.5 mm; Body_Flange_Dia=223.68 mm; Body_Flange_Dia_2=229.73 mm; Body_Height_1=212.5 mm; Body_Height_2=106.25 mm; Body_Height_3=94.5 mm; Body_Height_4=121.25 mm; Body_Top_Dia=26.56 mm; Body_Top_Dia_2=22.14 mm; Body_With_Dia=188.89 mm; Body_With_Dia_2=188.89 mm; Bolt_support=500 mm; Bolt_support_2=250 mm; Bolt_support_Dia=20 mm  [stored 0.0656168 ft]; Bolt_support_lenght=170.35 mm; Bolt_support_lenght_2=180.35 mm; Bottom_profile=75.18 mm; D1=185 mm; DN=300.7 mm; FOD=222.5 mm; Fillet_Length=10 mm  [stored 0.0328084 ft]; Flange_thickness=24.5 mm  [stored 0.0803806 ft]; H3=881 mm; ID=150.35 mm; L=850 mm; L1=867 mm; L_Ref=858.5 mm; L_ref_2=380.26 mm; PG_Dia=90 mm; PG_Ref=141.67 mm; PG_depth=14 mm  [stored 0.0459318 ft]; PG_ref=160.35 mm; Pilot_Dia_1=54.5 mm; Pilot_Dia_1_Ref=65.4 mm; Pilot_Dia_1_Ref_2=130.8 mm; Pilot_Dia_2=92.65 mm; Pilot_Dia_3=36.33 mm; Pilot_Dia_4=18.17 mm; Pilot_Dia_5=12.11 mm; Pilot_top_1=553.38 mm; Pilot_top_ref=105.13 mm; Profile1_Height=380 mm; Profile1_Length=76.72 mm; Profile1_Length_2=51.15 mm; Profile_Dia=10 mm  [stored 0.0328084 ft]; Profile_Dia_2=10 mm  [stored 0.0328084 ft]; Profile_Dia_3=20 mm  [stored 0.0656168 ft]; Top_Profile=300 mm; Top_Profile_Ref=305 mm; Top_Ref=448.25 mm; Top_Ref_2=500.81 mm; W=555 mm; W_Ref=462.35 mm
- 879-0300-00-14400207299_DN300_PN16: A=240.75 mm; Body_Collar_Dia=88.54 mm; Body_Collar_Dia_2=42.5 mm; Body_Flange_Dia=223.68 mm; Body_Flange_Dia_2=229.73 mm; Body_Height_1=212.5 mm; Body_Height_2=106.25 mm; Body_Height_3=94.5 mm; Body_Height_4=121.25 mm; Body_Top_Dia=26.56 mm; Body_Top_Dia_2=22.14 mm; Body_With_Dia=188.89 mm; Body_With_Dia_2=188.89 mm; Bolt_support=500 mm; Bolt_support_2=250 mm; Bolt_support_Dia=20 mm  [stored 0.0656168 ft]; Bolt_support_lenght=170.4 mm; Bolt_support_lenght_2=180.4 mm; Bottom_profile=75.2 mm; D1=185 mm; DN=300.8 mm; FOD=230 mm; Fillet_Length=10 mm  [stored 0.0328084 ft]; Flange_thickness=24.5 mm  [stored 0.0803806 ft]; H3=790 mm; ID=150.4 mm; L=850 mm; L1=867 mm; L_Ref=858.5 mm; L_ref_2=380.26 mm; PG_Dia=90 mm; PG_Ref=141.67 mm; PG_depth=14 mm  [stored 0.0459318 ft]; PG_ref=160.4 mm; Pilot_Dia_1=52.5 mm; Pilot_Dia_1_Ref=63 mm; Pilot_Dia_1_Ref_2=126 mm; Pilot_Dia_2=89.25 mm; Pilot_Dia_3=35 mm  [stored 0.114829 ft]; Pilot_Dia_4=17.5 mm  [stored 0.0574147 ft]; Pilot_Dia_5=11.67 mm; Pilot_top_1=504.13 mm; Pilot_top_ref=55.88 mm; Profile1_Height=361 mm; Profile1_Length=79.31 mm; Profile1_Length_2=52.87 mm; Profile_Dia=10 mm  [stored 0.0328084 ft]; Profile_Dia_2=10 mm  [stored 0.0328084 ft]; Profile_Dia_3=20 mm  [stored 0.0656168 ft]; Top_Profile=300 mm; Top_Profile_Ref=305 mm; Top_Ref=448.25 mm; Top_Ref_2=476.19 mm; W=555 mm; W_Ref=465.75 mm
- 879-0300-00-144002072A0_DN300_PN16: A=240.75 mm; Body_Collar_Dia=88.54 mm; Body_Collar_Dia_2=42.5 mm; Body_Flange_Dia=223.68 mm; Body_Flange_Dia_2=229.73 mm; Body_Height_1=212.5 mm; Body_Height_2=106.25 mm; Body_Height_3=106 mm; Body_Height_4=121.25 mm; Body_Top_Dia=26.56 mm; Body_Top_Dia_2=22.14 mm; Body_With_Dia=188.89 mm; Body_With_Dia_2=188.89 mm; Bolt_support=500 mm; Bolt_support_2=250 mm; Bolt_support_Dia=20 mm  [stored 0.0656168 ft]; Bolt_support_lenght=170.45 mm; Bolt_support_lenght_2=180.45 mm; Bottom_profile=75.23 mm; D1=185 mm; DN=300.9 mm; FOD=230 mm; Fillet_Length=10 mm  [stored 0.0328084 ft]; Flange_thickness=24.5 mm  [stored 0.0803806 ft]; H3=881 mm; ID=150.45 mm; L=850 mm; L1=867 mm; L_Ref=858.5 mm; L_ref_2=380.26 mm; PG_Dia=90 mm; PG_Ref=141.67 mm; PG_depth=14 mm  [stored 0.0459318 ft]; PG_ref=160.45 mm; Pilot_Dia_1=52.5 mm; Pilot_Dia_1_Ref=63 mm; Pilot_Dia_1_Ref_2=126 mm; Pilot_Dia_2=89.25 mm; Pilot_Dia_3=35 mm  [stored 0.114829 ft]; Pilot_Dia_4=17.5 mm  [stored 0.0574147 ft]; Pilot_Dia_5=11.67 mm; Pilot_top_1=555.38 mm; Pilot_top_ref=95.63 mm; Profile1_Height=400 mm; Profile1_Length=79.31 mm; Profile1_Length_2=52.87 mm; Profile_Dia=10 mm  [stored 0.0328084 ft]; Profile_Dia_2=10 mm  [stored 0.0328084 ft]; Profile_Dia_3=20 mm  [stored 0.0656168 ft]; Top_Profile=300 mm; Top_Profile_Ref=305 mm; Top_Ref=459.75 mm; Top_Ref_2=507.56 mm; W=555 mm; W_Ref=465.75 mm
- 879-0300-00-14400217299_DN300_PN16: A=237.35 mm; Body_Collar_Dia=88.54 mm; Body_Collar_Dia_2=42.5 mm; Body_Flange_Dia=223.68 mm; Body_Flange_Dia_2=229.73 mm; Body_Height_1=212.5 mm; Body_Height_2=106.25 mm; Body_Height_3=94.5 mm; Body_Height_4=121.25 mm; Body_Top_Dia=26.56 mm; Body_Top_Dia_2=22.14 mm; Body_With_Dia=188.89 mm; Body_With_Dia_2=188.89 mm; Bolt_support=500 mm; Bolt_support_2=250 mm; Bolt_support_Dia=20 mm  [stored 0.0656168 ft]; Bolt_support_lenght=170.06 mm; Bolt_support_lenght_2=180.06 mm; Bottom_profile=75.03 mm; D1=185 mm; DN=300.11 mm; FOD=230 mm; Fillet_Length=10 mm  [stored 0.0328084 ft]; Flange_thickness=24.5 mm  [stored 0.0803806 ft]; H3=790 mm; ID=150.06 mm; L=850 mm; L1=867 mm; L_Ref=858.5 mm; L_ref_2=380.26 mm; PG_Dia=90 mm; PG_Ref=141.67 mm; PG_depth=14 mm  [stored 0.0459318 ft]; PG_ref=160.06 mm; Pilot_Dia_1=54.5 mm; Pilot_Dia_1_Ref=65.4 mm; Pilot_Dia_1_Ref_2=130.8 mm; Pilot_Dia_2=92.65 mm; Pilot_Dia_3=36.33 mm; Pilot_Dia_4=18.17 mm; Pilot_Dia_5=12.11 mm; Pilot_top_1=504.13 mm; Pilot_top_ref=55.88 mm; Profile1_Height=380 mm; Profile1_Length=79.31 mm; Profile1_Length_2=52.87 mm; Profile_Dia=10 mm  [stored 0.0328084 ft]; Profile_Dia_2=10 mm  [stored 0.0328084 ft]; Profile_Dia_3=20 mm  [stored 0.0656168 ft]; Top_Profile=300 mm; Top_Profile_Ref=305 mm; Top_Ref=448.25 mm; Top_Ref_2=476.19 mm; W=555 mm; W_Ref=462.35 mm
- 879-0300-00-144002172A0_DN300_PN16: A=237.35 mm; Body_Collar_Dia=88.54 mm; Body_Collar_Dia_2=42.5 mm; Body_Flange_Dia=223.68 mm; Body_Flange_Dia_2=229.73 mm; Body_Height_1=212.5 mm; Body_Height_2=106.25 mm; Body_Height_3=94.5 mm; Body_Height_4=121.25 mm; Body_Top_Dia=26.56 mm; Body_Top_Dia_2=22.14 mm; Body_With_Dia=188.89 mm; Body_With_Dia_2=188.89 mm; Bolt_support=500 mm; Bolt_support_2=250 mm; Bolt_support_Dia=20 mm  [stored 0.0656168 ft]; Bolt_support_lenght=170.06 mm; Bolt_support_lenght_2=180.06 mm; Bottom_profile=75.03 mm; D1=185 mm; DN=300.12 mm; FOD=230 mm; Fillet_Length=10 mm  [stored 0.0328084 ft]; Flange_thickness=24.5 mm  [stored 0.0803806 ft]; H3=881 mm; ID=150.06 mm; L=850 mm; L1=867 mm; L_Ref=858.5 mm; L_ref_2=380.26 mm; PG_Dia=90 mm; PG_Ref=141.67 mm; PG_depth=14 mm  [stored 0.0459318 ft]; PG_ref=160.06 mm; Pilot_Dia_1=54.5 mm; Pilot_Dia_1_Ref=65.4 mm; Pilot_Dia_1_Ref_2=130.8 mm; Pilot_Dia_2=92.65 mm; Pilot_Dia_3=36.33 mm; Pilot_Dia_4=18.17 mm; Pilot_Dia_5=12.11 mm; Pilot_top_1=549.63 mm; Pilot_top_ref=101.38 mm; Profile1_Height=380 mm; Profile1_Length=79.31 mm; Profile1_Length_2=52.87 mm; Profile_Dia=10 mm  [stored 0.0328084 ft]; Profile_Dia_2=10 mm  [stored 0.0328084 ft]; Profile_Dia_3=20 mm  [stored 0.0656168 ft]; Top_Profile=300 mm; Top_Profile_Ref=305 mm; Top_Ref=448.25 mm; Top_Ref_2=498.94 mm; W=555 mm; W_Ref=462.35 mm
- 879-0300-00-14400227299_DN300_PN16: A=240.75 mm; Body_Collar_Dia=88.54 mm; Body_Collar_Dia_2=42.5 mm; Body_Flange_Dia=223.68 mm; Body_Flange_Dia_2=229.73 mm; Body_Height_1=212.5 mm; Body_Height_2=106.25 mm; Body_Height_3=94.5 mm; Body_Height_4=121.25 mm; Body_Top_Dia=26.56 mm; Body_Top_Dia_2=22.14 mm; Body_With_Dia=188.89 mm; Body_With_Dia_2=188.89 mm; Bolt_support=500 mm; Bolt_support_2=250 mm; Bolt_support_Dia=20 mm  [stored 0.0656168 ft]; Bolt_support_lenght=170.07 mm; Bolt_support_lenght_2=180.07 mm; Bottom_profile=75.03 mm; D1=185 mm; DN=300.13 mm; FOD=230 mm; Fillet_Length=10 mm  [stored 0.0328084 ft]; Flange_thickness=24.5 mm  [stored 0.0803806 ft]; H3=790 mm; ID=150.07 mm; L=850 mm; L1=867 mm; L_Ref=858.5 mm; L_ref_2=380.26 mm; PG_Dia=90 mm; PG_Ref=141.67 mm; PG_depth=14 mm  [stored 0.0459318 ft]; PG_ref=160.07 mm; Pilot_Dia_1=52.5 mm; Pilot_Dia_1_Ref=63 mm; Pilot_Dia_1_Ref_2=126 mm; Pilot_Dia_2=89.25 mm; Pilot_Dia_3=35 mm  [stored 0.114829 ft]; Pilot_Dia_4=17.5 mm  [stored 0.0574147 ft]; Pilot_Dia_5=11.67 mm; Pilot_top_1=504.13 mm; Pilot_top_ref=55.88 mm; Profile1_Height=361 mm; Profile1_Length=79.31 mm; Profile1_Length_2=52.87 mm; Profile_Dia=10 mm  [stored 0.0328084 ft]; Profile_Dia_2=10 mm  [stored 0.0328084 ft]; Profile_Dia_3=20 mm  [stored 0.0656168 ft]; Top_Profile=300 mm; Top_Profile_Ref=305 mm; Top_Ref=448.25 mm; Top_Ref_2=476.19 mm; W=555 mm; W_Ref=465.75 mm
- 879-0300-00-144002272A0_DN300_PN16: A=240.75 mm; Body_Collar_Dia=88.54 mm; Body_Collar_Dia_2=42.5 mm; Body_Flange_Dia=223.68 mm; Body_Flange_Dia_2=229.73 mm; Body_Height_1=212.5 mm; Body_Height_2=106.25 mm; Body_Height_3=106 mm; Body_Height_4=121.25 mm; Body_Top_Dia=26.56 mm; Body_Top_Dia_2=22.14 mm; Body_With_Dia=188.89 mm; Body_With_Dia_2=188.89 mm; Bolt_support=500 mm; Bolt_support_2=250 mm; Bolt_support_Dia=20 mm  [stored 0.0656168 ft]; Bolt_support_lenght=170.07 mm; Bolt_support_lenght_2=180.07 mm; Bottom_profile=75.04 mm; D1=185 mm; DN=300.14 mm; FOD=230 mm; Fillet_Length=10 mm  [stored 0.0328084 ft]; Flange_thickness=24.5 mm  [stored 0.0803806 ft]; H3=881 mm; ID=150.07 mm; L=850 mm; L1=867 mm; L_Ref=858.5 mm; L_ref_2=380.26 mm; PG_Dia=90 mm; PG_Ref=141.67 mm; PG_depth=14 mm  [stored 0.0459318 ft]; PG_ref=160.07 mm; Pilot_Dia_1=52.5 mm; Pilot_Dia_1_Ref=63 mm; Pilot_Dia_1_Ref_2=126 mm; Pilot_Dia_2=89.25 mm; Pilot_Dia_3=35 mm  [stored 0.114829 ft]; Pilot_Dia_4=17.5 mm  [stored 0.0574147 ft]; Pilot_Dia_5=11.67 mm; Pilot_top_1=555.38 mm; Pilot_top_ref=95.63 mm; Profile1_Height=400 mm; Profile1_Length=79.31 mm; Profile1_Length_2=52.87 mm; Profile_Dia=10 mm  [stored 0.0328084 ft]; Profile_Dia_2=10 mm  [stored 0.0328084 ft]; Profile_Dia_3=20 mm  [stored 0.0656168 ft]; Top_Profile=300 mm; Top_Profile_Ref=305 mm; Top_Ref=459.75 mm; Top_Ref_2=507.56 mm; W=555 mm; W_Ref=465.75 mm
- 879-0300-00-14400237299_DN300_PN16: A=237.35 mm; Body_Collar_Dia=88.54 mm; Body_Collar_Dia_2=42.5 mm; Body_Flange_Dia=223.68 mm; Body_Flange_Dia_2=229.73 mm; Body_Height_1=212.5 mm; Body_Height_2=106.25 mm; Body_Height_3=94.5 mm; Body_Height_4=121.25 mm; Body_Top_Dia=26.56 mm; Body_Top_Dia_2=22.14 mm; Body_With_Dia=188.89 mm; Body_With_Dia_2=188.89 mm; Bolt_support=500 mm; Bolt_support_2=250 mm; Bolt_support_Dia=20 mm  [stored 0.0656168 ft]; Bolt_support_lenght=170.08 mm; Bolt_support_lenght_2=180.08 mm; Bottom_profile=75.04 mm; D1=185 mm; DN=300.15 mm; FOD=230 mm; Fillet_Length=10 mm  [stored 0.0328084 ft]; Flange_thickness=24.5 mm  [stored 0.0803806 ft]; H3=790 mm; ID=150.08 mm; L=850 mm; L1=867 mm; L_Ref=858.5 mm; L_ref_2=380.26 mm; PG_Dia=90 mm; PG_Ref=141.67 mm; PG_depth=14 mm  [stored 0.0459318 ft]; PG_ref=160.08 mm; Pilot_Dia_1=54.5 mm; Pilot_Dia_1_Ref=65.4 mm; Pilot_Dia_1_Ref_2=130.8 mm; Pilot_Dia_2=92.65 mm; Pilot_Dia_3=36.33 mm; Pilot_Dia_4=18.17 mm; Pilot_Dia_5=12.11 mm; Pilot_top_1=504.13 mm; Pilot_top_ref=55.88 mm; Profile1_Height=380 mm; Profile1_Length=79.31 mm; Profile1_Length_2=52.87 mm; Profile_Dia=10 mm  [stored 0.0328084 ft]; Profile_Dia_2=10 mm  [stored 0.0328084 ft]; Profile_Dia_3=20 mm  [stored 0.0656168 ft]; Top_Profile=300 mm; Top_Profile_Ref=305 mm; Top_Ref=448.25 mm; Top_Ref_2=476.19 mm; W=555 mm; W_Ref=462.35 mm
- 879-0300-00-144002372A0_DN300_PN16: A=237.35 mm; Body_Collar_Dia=88.54 mm; Body_Collar_Dia_2=42.5 mm; Body_Flange_Dia=223.68 mm; Body_Flange_Dia_2=229.73 mm; Body_Height_1=212.5 mm; Body_Height_2=106.25 mm; Body_Height_3=94.5 mm; Body_Height_4=121.25 mm; Body_Top_Dia=26.56 mm; Body_Top_Dia_2=22.14 mm; Body_With_Dia=188.89 mm; Body_With_Dia_2=188.89 mm; Bolt_support=500 mm; Bolt_support_2=250 mm; Bolt_support_Dia=20 mm  [stored 0.0656168 ft]; Bolt_support_lenght=170.08 mm; Bolt_support_lenght_2=180.08 mm; Bottom_profile=75.04 mm; D1=185 mm; DN=300.16 mm; FOD=230 mm; Fillet_Length=10 mm  [stored 0.0328084 ft]; Flange_thickness=24.5 mm  [stored 0.0803806 ft]; H3=881 mm; ID=150.08 mm; L=850 mm; L1=867 mm; L_Ref=858.5 mm; L_ref_2=380.26 mm; PG_Dia=90 mm; PG_Ref=141.67 mm; PG_depth=14 mm  [stored 0.0459318 ft]; PG_ref=160.08 mm; Pilot_Dia_1=54.5 mm; Pilot_Dia_1_Ref=65.4 mm; Pilot_Dia_1_Ref_2=130.8 mm; Pilot_Dia_2=92.65 mm; Pilot_Dia_3=36.33 mm; Pilot_Dia_4=18.17 mm; Pilot_Dia_5=12.11 mm; Pilot_top_1=549.63 mm; Pilot_top_ref=101.38 mm; Profile1_Height=380 mm; Profile1_Length=79.31 mm; Profile1_Length_2=52.87 mm; Profile_Dia=10 mm  [stored 0.0328084 ft]; Profile_Dia_2=10 mm  [stored 0.0328084 ft]; Profile_Dia_3=20 mm  [stored 0.0656168 ft]; Top_Profile=300 mm; Top_Profile_Ref=305 mm; Top_Ref=448.25 mm; Top_Ref_2=498.94 mm; W=555 mm; W_Ref=462.35 mm
- 879-0350-00-04400207299_DN350_PN10: A=257.15 mm; Body_Collar_Dia=102.08 mm; Body_Collar_Dia_2=49 mm; Body_Flange_Dia=257.89 mm; Body_Flange_Dia_2=264.86 mm; Body_Height_1=245 mm; Body_Height_2=122.5 mm; Body_Height_3=98 mm; Body_Height_4=137.5 mm; Body_Top_Dia=30.63 mm; Body_Top_Dia_2=25.52 mm; Body_With_Dia=217.78 mm; Body_With_Dia_2=217.78 mm; Bolt_support=576.47 mm; Bolt_support_2=288.24 mm; Bolt_support_Dia=30 mm  [stored 0.0984252 ft]; Bolt_support_lenght=195 mm; Bolt_support_lenght_2=205 mm; Bottom_profile=87.5 mm; D1=214.5 mm; DN=350 mm; FOD=252.5 mm; Fillet_Length=15 mm  [stored 0.0492126 ft]; Flange_thickness=26.5 mm  [stored 0.0869423 ft]; H3=875 mm; ID=175 mm; L=980 mm; L1=997 mm; L_Ref=988.5 mm; L_ref_2=440.17 mm; PG_Dia=110 mm; PG_Ref=163.33 mm; PG_depth=21 mm  [stored 0.0688976 ft]; PG_ref=185 mm; Pilot_Dia_1=60.5 mm; Pilot_Dia_1_Ref=72.6 mm; Pilot_Dia_1_Ref_2=145.2 mm; Pilot_Dia_2=102.85 mm; Pilot_Dia_3=40.33 mm; Pilot_Dia_4=20.17 mm; Pilot_Dia_5=13.44 mm; Pilot_top_1=561.5 mm; Pilot_top_ref=61 mm; Profile1_Height=430 mm; Profile1_Length=87.07 mm; Profile1_Length_2=58.05 mm; Profile_Dia=15 mm  [stored 0.0492126 ft]; Profile_Dia_2=15 mm  [stored 0.0492126 ft]; Profile_Dia_3=30 mm  [stored 0.0984252 ft]; Top_Profile=345.88 mm; Top_Profile_Ref=350.88 mm; Top_Ref=500.5 mm; Top_Ref_2=531 mm; W=605 mm; W_Ref=502.15 mm
- 879-0350-00-044002072A0_DN350_PN10: A=257.15 mm; Body_Collar_Dia=102.08 mm; Body_Collar_Dia_2=49 mm; Body_Flange_Dia=257.89 mm; Body_Flange_Dia_2=264.86 mm; Body_Height_1=245 mm; Body_Height_2=122.5 mm; Body_Height_3=98 mm; Body_Height_4=137.5 mm; Body_Top_Dia=30.63 mm; Body_Top_Dia_2=25.52 mm; Body_With_Dia=217.78 mm; Body_With_Dia_2=217.78 mm; Bolt_support=576.47 mm; Bolt_support_2=288.24 mm; Bolt_support_Dia=30 mm  [stored 0.0984252 ft]; Bolt_support_lenght=195.05 mm; Bolt_support_lenght_2=205.05 mm; Bottom_profile=87.53 mm; D1=214.5 mm; DN=350.1 mm; FOD=252.5 mm; Fillet_Length=15 mm  [stored 0.0492126 ft]; Flange_thickness=26.5 mm  [stored 0.0869423 ft]; H3=959 mm; ID=175.05 mm; L=980 mm; L1=997 mm; L_Ref=988.5 mm; L_ref_2=440.17 mm; PG_Dia=110 mm; PG_Ref=163.33 mm; PG_depth=21 mm  [stored 0.0688976 ft]; PG_ref=185.05 mm; Pilot_Dia_1=60.5 mm; Pilot_Dia_1_Ref=72.6 mm; Pilot_Dia_1_Ref_2=145.2 mm; Pilot_Dia_2=102.85 mm; Pilot_Dia_3=40.33 mm; Pilot_Dia_4=20.17 mm; Pilot_Dia_5=13.44 mm; Pilot_top_1=603.5 mm; Pilot_top_ref=103 mm; Profile1_Height=430 mm; Profile1_Length=87.07 mm; Profile1_Length_2=58.05 mm; Profile_Dia=15 mm  [stored 0.0492126 ft]; Profile_Dia_2=15 mm  [stored 0.0492126 ft]; Profile_Dia_3=30 mm  [stored 0.0984252 ft]; Top_Profile=345.88 mm; Top_Profile_Ref=350.88 mm; Top_Ref=500.5 mm; Top_Ref_2=552 mm; W=605 mm; W_Ref=502.15 mm
- 879-0350-00-04400217299_DN350_PN10: A=252.9 mm; Body_Collar_Dia=102.08 mm; Body_Collar_Dia_2=49 mm; Body_Flange_Dia=257.89 mm; Body_Flange_Dia_2=264.86 mm; Body_Height_1=245 mm; Body_Height_2=122.5 mm; Body_Height_3=89 mm; Body_Height_4=137.5 mm; Body_Top_Dia=30.63 mm; Body_Top_Dia_2=25.52 mm; Body_With_Dia=217.78 mm; Body_With_Dia_2=217.78 mm; Bolt_support=576.47 mm; Bolt_support_2=288.24 mm; Bolt_support_Dia=30 mm  [stored 0.0984252 ft]; Bolt_support_lenght=195.1 mm; Bolt_support_lenght_2=205.1 mm; Bottom_profile=87.55 mm; D1=214.5 mm; DN=350.2 mm; FOD=252.5 mm; Fillet_Length=15 mm  [stored 0.0492126 ft]; Flange_thickness=26.5 mm  [stored 0.0869423 ft]; H3=875 mm; ID=175.1 mm; L=980 mm; L1=997 mm; L_Ref=988.5 mm; L_ref_2=440.17 mm; PG_Dia=110 mm; PG_Ref=163.33 mm; PG_depth=21 mm  [stored 0.0688976 ft]; PG_ref=185.1 mm; Pilot_Dia_1=63 mm; Pilot_Dia_1_Ref=75.6 mm; Pilot_Dia_1_Ref_2=151.2 mm; Pilot_Dia_2=107.1 mm; Pilot_Dia_3=42 mm; Pilot_Dia_4=21 mm  [stored 0.0688976 ft]; Pilot_Dia_5=14 mm  [stored 0.0459318 ft]; Pilot_top_1=557 mm; Pilot_top_ref=65.5 mm; Profile1_Height=430 mm; Profile1_Length=87.07 mm; Profile1_Length_2=58.05 mm; Profile_Dia=15 mm  [stored 0.0492126 ft]; Profile_Dia_2=15 mm  [stored 0.0492126 ft]; Profile_Dia_3=30 mm  [stored 0.0984252 ft]; Top_Profile=345.88 mm; Top_Profile_Ref=350.88 mm; Top_Ref=491.5 mm; Top_Ref_2=524.25 mm; W=605 mm; W_Ref=497.9 mm
- 879-0350-00-044002172A0_DN350_PN10: A=252.9 mm; Body_Collar_Dia=102.08 mm; Body_Collar_Dia_2=49 mm; Body_Flange_Dia=257.89 mm; Body_Flange_Dia_2=264.86 mm; Body_Height_1=245 mm; Body_Height_2=122.5 mm; Body_Height_3=89 mm; Body_Height_4=137.5 mm; Body_Top_Dia=30.63 mm; Body_Top_Dia_2=25.52 mm; Body_With_Dia=217.78 mm; Body_With_Dia_2=217.78 mm; Bolt_support=576.47 mm; Bolt_support_2=288.24 mm; Bolt_support_Dia=30 mm  [stored 0.0984252 ft]; Bolt_support_lenght=195.15 mm; Bolt_support_lenght_2=205.15 mm; Bottom_profile=87.58 mm; D1=214.5 mm; DN=350.3 mm; FOD=252.5 mm; Fillet_Length=15 mm  [stored 0.0492126 ft]; Flange_thickness=26.5 mm  [stored 0.0869423 ft]; H3=959 mm; ID=175.15 mm; L=980 mm; L1=997 mm; L_Ref=988.5 mm; L_ref_2=440.17 mm; PG_Dia=110 mm; PG_Ref=163.33 mm; PG_depth=21 mm  [stored 0.0688976 ft]; PG_ref=185.15 mm; Pilot_Dia_1=63 mm; Pilot_Dia_1_Ref=75.6 mm; Pilot_Dia_1_Ref_2=151.2 mm; Pilot_Dia_2=107.1 mm; Pilot_Dia_3=42 mm; Pilot_Dia_4=21 mm  [stored 0.0688976 ft]; Pilot_Dia_5=14 mm  [stored 0.0459318 ft]; Pilot_top_1=599 mm; Pilot_top_ref=107.5 mm; Profile1_Height=430 mm; Profile1_Length=87.07 mm; Profile1_Length_2=58.05 mm; Profile_Dia=15 mm  [stored 0.0492126 ft]; Profile_Dia_2=15 mm  [stored 0.0492126 ft]; Profile_Dia_3=30 mm  [stored 0.0984252 ft]; Top_Profile=345.88 mm; Top_Profile_Ref=350.88 mm; Top_Ref=491.5 mm; Top_Ref_2=545.25 mm; W=605 mm; W_Ref=497.9 mm
- 879-0350-00-04400227299_DN350_PN10: A=257.15 mm; Body_Collar_Dia=102.08 mm; Body_Collar_Dia_2=49 mm; Body_Flange_Dia=257.89 mm; Body_Flange_Dia_2=264.86 mm; Body_Height_1=245 mm; Body_Height_2=122.5 mm; Body_Height_3=98 mm; Body_Height_4=137.5 mm; Body_Top_Dia=30.63 mm; Body_Top_Dia_2=25.52 mm; Body_With_Dia=217.78 mm; Body_With_Dia_2=217.78 mm; Bolt_support=576.47 mm; Bolt_support_2=288.24 mm; Bolt_support_Dia=30 mm  [stored 0.0984252 ft]; Bolt_support_lenght=195.2 mm; Bolt_support_lenght_2=205.2 mm; Bottom_profile=87.6 mm; D1=214.5 mm; DN=350.4 mm; FOD=252.5 mm; Fillet_Length=15 mm  [stored 0.0492126 ft]; Flange_thickness=26.5 mm  [stored 0.0869423 ft]; H3=875 mm; ID=175.2 mm; L=980 mm; L1=997 mm; L_Ref=988.5 mm; L_ref_2=440.17 mm; PG_Dia=110 mm; PG_Ref=163.33 mm; PG_depth=21 mm  [stored 0.0688976 ft]; PG_ref=185.2 mm; Pilot_Dia_1=60.5 mm; Pilot_Dia_1_Ref=72.6 mm; Pilot_Dia_1_Ref_2=145.2 mm; Pilot_Dia_2=102.85 mm; Pilot_Dia_3=40.33 mm; Pilot_Dia_4=20.17 mm; Pilot_Dia_5=13.44 mm; Pilot_top_1=561.5 mm; Pilot_top_ref=61 mm; Profile1_Height=430 mm; Profile1_Length=87.07 mm; Profile1_Length_2=58.05 mm; Profile_Dia=15 mm  [stored 0.0492126 ft]; Profile_Dia_2=15 mm  [stored 0.0492126 ft]; Profile_Dia_3=30 mm  [stored 0.0984252 ft]; Top_Profile=345.88 mm; Top_Profile_Ref=350.88 mm; Top_Ref=500.5 mm; Top_Ref_2=531 mm; W=605 mm; W_Ref=502.15 mm
- 879-0350-00-044002272A0_DN350_PN10: A=257.15 mm; Body_Collar_Dia=102.08 mm; Body_Collar_Dia_2=49 mm; Body_Flange_Dia=257.89 mm; Body_Flange_Dia_2=264.86 mm; Body_Height_1=245 mm; Body_Height_2=122.5 mm; Body_Height_3=98 mm; Body_Height_4=137.5 mm; Body_Top_Dia=30.63 mm; Body_Top_Dia_2=25.52 mm; Body_With_Dia=217.78 mm; Body_With_Dia_2=217.78 mm; Bolt_support=576.47 mm; Bolt_support_2=288.24 mm; Bolt_support_Dia=30 mm  [stored 0.0984252 ft]; Bolt_support_lenght=195.25 mm; Bolt_support_lenght_2=205.25 mm; Bottom_profile=87.63 mm; D1=214.5 mm; DN=350.5 mm; FOD=252.5 mm; Fillet_Length=15 mm  [stored 0.0492126 ft]; Flange_thickness=26.5 mm  [stored 0.0869423 ft]; H3=959 mm; ID=175.25 mm; L=980 mm; L1=997 mm; L_Ref=988.5 mm; L_ref_2=440.17 mm; PG_Dia=110 mm; PG_Ref=163.33 mm; PG_depth=21 mm  [stored 0.0688976 ft]; PG_ref=185.25 mm; Pilot_Dia_1=60.5 mm; Pilot_Dia_1_Ref=72.6 mm; Pilot_Dia_1_Ref_2=145.2 mm; Pilot_Dia_2=102.85 mm; Pilot_Dia_3=40.33 mm; Pilot_Dia_4=20.17 mm; Pilot_Dia_5=13.44 mm; Pilot_top_1=603.5 mm; Pilot_top_ref=103 mm; Profile1_Height=430 mm; Profile1_Length=87.07 mm; Profile1_Length_2=58.05 mm; Profile_Dia=15 mm  [stored 0.0492126 ft]; Profile_Dia_2=15 mm  [stored 0.0492126 ft]; Profile_Dia_3=30 mm  [stored 0.0984252 ft]; Top_Profile=345.88 mm; Top_Profile_Ref=350.88 mm; Top_Ref=500.5 mm; Top_Ref_2=552 mm; W=605 mm; W_Ref=502.15 mm
- 879-0350-00-04400237299_DN350_PN10: A=252.9 mm; Body_Collar_Dia=102.08 mm; Body_Collar_Dia_2=49 mm; Body_Flange_Dia=257.89 mm; Body_Flange_Dia_2=264.86 mm; Body_Height_1=245 mm; Body_Height_2=122.5 mm; Body_Height_3=89 mm; Body_Height_4=137.5 mm; Body_Top_Dia=30.63 mm; Body_Top_Dia_2=25.52 mm; Body_With_Dia=217.78 mm; Body_With_Dia_2=217.78 mm; Bolt_support=576.47 mm; Bolt_support_2=288.24 mm; Bolt_support_Dia=30 mm  [stored 0.0984252 ft]; Bolt_support_lenght=195.3 mm; Bolt_support_lenght_2=205.3 mm; Bottom_profile=87.65 mm; D1=214.5 mm; DN=350.6 mm; FOD=252.5 mm; Fillet_Length=15 mm  [stored 0.0492126 ft]; Flange_thickness=26.5 mm  [stored 0.0869423 ft]; H3=875 mm; ID=175.3 mm; L=980 mm; L1=997 mm; L_Ref=988.5 mm; L_ref_2=440.17 mm; PG_Dia=110 mm; PG_Ref=163.33 mm; PG_depth=21 mm  [stored 0.0688976 ft]; PG_ref=185.3 mm; Pilot_Dia_1=63 mm; Pilot_Dia_1_Ref=75.6 mm; Pilot_Dia_1_Ref_2=151.2 mm; Pilot_Dia_2=107.1 mm; Pilot_Dia_3=42 mm; Pilot_Dia_4=21 mm  [stored 0.0688976 ft]; Pilot_Dia_5=14 mm  [stored 0.0459318 ft]; Pilot_top_1=557 mm; Pilot_top_ref=65.5 mm; Profile1_Height=430 mm; Profile1_Length=87.07 mm; Profile1_Length_2=58.05 mm; Profile_Dia=15 mm  [stored 0.0492126 ft]; Profile_Dia_2=15 mm  [stored 0.0492126 ft]; Profile_Dia_3=30 mm  [stored 0.0984252 ft]; Top_Profile=345.88 mm; Top_Profile_Ref=350.88 mm; Top_Ref=491.5 mm; Top_Ref_2=524.25 mm; W=605 mm; W_Ref=497.9 mm
- 879-0350-00-044002372A0_DN350_PN10: A=252.9 mm; Body_Collar_Dia=102.08 mm; Body_Collar_Dia_2=49 mm; Body_Flange_Dia=257.89 mm; Body_Flange_Dia_2=264.86 mm; Body_Height_1=245 mm; Body_Height_2=122.5 mm; Body_Height_3=89 mm; Body_Height_4=137.5 mm; Body_Top_Dia=30.63 mm; Body_Top_Dia_2=25.52 mm; Body_With_Dia=217.78 mm; Body_With_Dia_2=217.78 mm; Bolt_support=576.47 mm; Bolt_support_2=288.24 mm; Bolt_support_Dia=30 mm  [stored 0.0984252 ft]; Bolt_support_lenght=195.35 mm; Bolt_support_lenght_2=205.35 mm; Bottom_profile=87.68 mm; D1=214.5 mm; DN=350.7 mm; FOD=252.5 mm; Fillet_Length=15 mm  [stored 0.0492126 ft]; Flange_thickness=26.5 mm  [stored 0.0869423 ft]; H3=959 mm; ID=175.35 mm; L=980 mm; L1=997 mm; L_Ref=988.5 mm; L_ref_2=440.17 mm; PG_Dia=110 mm; PG_Ref=163.33 mm; PG_depth=21 mm  [stored 0.0688976 ft]; PG_ref=185.35 mm; Pilot_Dia_1=63 mm; Pilot_Dia_1_Ref=75.6 mm; Pilot_Dia_1_Ref_2=151.2 mm; Pilot_Dia_2=107.1 mm; Pilot_Dia_3=42 mm; Pilot_Dia_4=21 mm  [stored 0.0688976 ft]; Pilot_Dia_5=14 mm  [stored 0.0459318 ft]; Pilot_top_1=599 mm; Pilot_top_ref=107.5 mm; Profile1_Height=430 mm; Profile1_Length=87.07 mm; Profile1_Length_2=58.05 mm; Profile_Dia=15 mm  [stored 0.0492126 ft]; Profile_Dia_2=15 mm  [stored 0.0492126 ft]; Profile_Dia_3=30 mm  [stored 0.0984252 ft]; Top_Profile=345.88 mm; Top_Profile_Ref=350.88 mm; Top_Ref=491.5 mm; Top_Ref_2=545.25 mm; W=605 mm; W_Ref=497.9 mm
- 879-0350-00-14400207299_DN350_PN16: A=249.65 mm; Body_Collar_Dia=102.08 mm; Body_Collar_Dia_2=49 mm; Body_Flange_Dia=257.89 mm; Body_Flange_Dia_2=264.86 mm; Body_Height_1=245 mm; Body_Height_2=122.5 mm; Body_Height_3=98 mm; Body_Height_4=137.5 mm; Body_Top_Dia=30.63 mm; Body_Top_Dia_2=25.52 mm; Body_With_Dia=217.78 mm; Body_With_Dia_2=217.78 mm; Bolt_support=576.47 mm; Bolt_support_2=288.24 mm; Bolt_support_Dia=30 mm  [stored 0.0984252 ft]; Bolt_support_lenght=195.4 mm; Bolt_support_lenght_2=205.4 mm; Bottom_profile=87.7 mm; D1=214.5 mm; DN=350.8 mm; FOD=260 mm; Fillet_Length=15 mm  [stored 0.0492126 ft]; Flange_thickness=26.5 mm  [stored 0.0869423 ft]; H3=875 mm; ID=175.4 mm; L=980 mm; L1=997 mm; L_Ref=988.5 mm; L_ref_2=440.17 mm; PG_Dia=110 mm; PG_Ref=163.33 mm; PG_depth=21 mm  [stored 0.0688976 ft]; PG_ref=185.4 mm; Pilot_Dia_1=60.5 mm; Pilot_Dia_1_Ref=72.6 mm; Pilot_Dia_1_Ref_2=145.2 mm; Pilot_Dia_2=102.85 mm; Pilot_Dia_3=40.33 mm; Pilot_Dia_4=20.17 mm; Pilot_Dia_5=13.44 mm; Pilot_top_1=557.75 mm; Pilot_top_ref=57.25 mm; Profile1_Height=430 mm; Profile1_Length=89.66 mm; Profile1_Length_2=59.77 mm; Profile_Dia=15 mm  [stored 0.0492126 ft]; Profile_Dia_2=15 mm  [stored 0.0492126 ft]; Profile_Dia_3=30 mm  [stored 0.0984252 ft]; Top_Profile=345.88 mm; Top_Profile_Ref=350.88 mm; Top_Ref=500.5 mm; Top_Ref_2=529.13 mm; W=605 mm; W_Ref=502.15 mm
- 879-0350-00-144002072A0_DN350_PN16: A=249.65 mm; Body_Collar_Dia=102.08 mm; Body_Collar_Dia_2=49 mm; Body_Flange_Dia=257.89 mm; Body_Flange_Dia_2=264.86 mm; Body_Height_1=245 mm; Body_Height_2=122.5 mm; Body_Height_3=98 mm; Body_Height_4=137.5 mm; Body_Top_Dia=30.63 mm; Body_Top_Dia_2=25.52 mm; Body_With_Dia=217.78 mm; Body_With_Dia_2=217.78 mm; Bolt_support=576.47 mm; Bolt_support_2=288.24 mm; Bolt_support_Dia=30 mm  [stored 0.0984252 ft]; Bolt_support_lenght=195.45 mm; Bolt_support_lenght_2=205.45 mm; Bottom_profile=87.73 mm; D1=214.5 mm; DN=350.9 mm; FOD=260 mm; Fillet_Length=15 mm  [stored 0.0492126 ft]; Flange_thickness=26.5 mm  [stored 0.0869423 ft]; H3=959 mm; ID=175.45 mm; L=980 mm; L1=997 mm; L_Ref=988.5 mm; L_ref_2=440.17 mm; PG_Dia=110 mm; PG_Ref=163.33 mm; PG_depth=21 mm  [stored 0.0688976 ft]; PG_ref=185.45 mm; Pilot_Dia_1=60.5 mm; Pilot_Dia_1_Ref=72.6 mm; Pilot_Dia_1_Ref_2=145.2 mm; Pilot_Dia_2=102.85 mm; Pilot_Dia_3=40.33 mm; Pilot_Dia_4=20.17 mm; Pilot_Dia_5=13.44 mm; Pilot_top_1=599.75 mm; Pilot_top_ref=99.25 mm; Profile1_Height=430 mm; Profile1_Length=89.66 mm; Profile1_Length_2=59.77 mm; Profile_Dia=15 mm  [stored 0.0492126 ft]; Profile_Dia_2=15 mm  [stored 0.0492126 ft]; Profile_Dia_3=30 mm  [stored 0.0984252 ft]; Top_Profile=345.88 mm; Top_Profile_Ref=350.88 mm; Top_Ref=500.5 mm; Top_Ref_2=550.13 mm; W=605 mm; W_Ref=502.15 mm
- 879-0350-00-14400217299_DN350_PN16: A=245.4 mm; Body_Collar_Dia=102.08 mm; Body_Collar_Dia_2=49 mm; Body_Flange_Dia=257.89 mm; Body_Flange_Dia_2=264.86 mm; Body_Height_1=245 mm; Body_Height_2=122.5 mm; Body_Height_3=89 mm; Body_Height_4=137.5 mm; Body_Top_Dia=30.63 mm; Body_Top_Dia_2=25.52 mm; Body_With_Dia=217.78 mm; Body_With_Dia_2=217.78 mm; Bolt_support=576.47 mm; Bolt_support_2=288.24 mm; Bolt_support_Dia=30 mm  [stored 0.0984252 ft]; Bolt_support_lenght=195.06 mm; Bolt_support_lenght_2=205.06 mm; Bottom_profile=87.53 mm; D1=214.5 mm; DN=350.11 mm; FOD=260 mm; Fillet_Length=15 mm  [stored 0.0492126 ft]; Flange_thickness=26.5 mm  [stored 0.0869423 ft]; H3=875 mm; ID=175.06 mm; L=980 mm; L1=997 mm; L_Ref=988.5 mm; L_ref_2=440.17 mm; PG_Dia=110 mm; PG_Ref=163.33 mm; PG_depth=21 mm  [stored 0.0688976 ft]; PG_ref=185.06 mm; Pilot_Dia_1=63 mm; Pilot_Dia_1_Ref=75.6 mm; Pilot_Dia_1_Ref_2=151.2 mm; Pilot_Dia_2=107.1 mm; Pilot_Dia_3=42 mm; Pilot_Dia_4=21 mm  [stored 0.0688976 ft]; Pilot_Dia_5=14 mm  [stored 0.0459318 ft]; Pilot_top_1=553.25 mm; Pilot_top_ref=61.75 mm; Profile1_Height=430 mm; Profile1_Length=89.66 mm; Profile1_Length_2=59.77 mm; Profile_Dia=15 mm  [stored 0.0492126 ft]; Profile_Dia_2=15 mm  [stored 0.0492126 ft]; Profile_Dia_3=30 mm  [stored 0.0984252 ft]; Top_Profile=345.88 mm; Top_Profile_Ref=350.88 mm; Top_Ref=491.5 mm; Top_Ref_2=522.38 mm; W=605 mm; W_Ref=497.9 mm
- 879-0350-00-144002172A0_DN350_PN16: A=245.4 mm; Body_Collar_Dia=102.08 mm; Body_Collar_Dia_2=49 mm; Body_Flange_Dia=257.89 mm; Body_Flange_Dia_2=264.86 mm; Body_Height_1=245 mm; Body_Height_2=122.5 mm; Body_Height_3=89 mm; Body_Height_4=137.5 mm; Body_Top_Dia=30.63 mm; Body_Top_Dia_2=25.52 mm; Body_With_Dia=217.78 mm; Body_With_Dia_2=217.78 mm; Bolt_support=576.47 mm; Bolt_support_2=288.24 mm; Bolt_support_Dia=30 mm  [stored 0.0984252 ft]; Bolt_support_lenght=195.06 mm; Bolt_support_lenght_2=205.06 mm; Bottom_profile=87.53 mm; D1=214.5 mm; DN=350.12 mm; FOD=260 mm; Fillet_Length=15 mm  [stored 0.0492126 ft]; Flange_thickness=26.5 mm  [stored 0.0869423 ft]; H3=959 mm; ID=175.06 mm; L=980 mm; L1=997 mm; L_Ref=988.5 mm; L_ref_2=440.17 mm; PG_Dia=110 mm; PG_Ref=163.33 mm; PG_depth=21 mm  [stored 0.0688976 ft]; PG_ref=185.06 mm; Pilot_Dia_1=63 mm; Pilot_Dia_1_Ref=75.6 mm; Pilot_Dia_1_Ref_2=151.2 mm; Pilot_Dia_2=107.1 mm; Pilot_Dia_3=42 mm; Pilot_Dia_4=21 mm  [stored 0.0688976 ft]; Pilot_Dia_5=14 mm  [stored 0.0459318 ft]; Pilot_top_1=595.25 mm; Pilot_top_ref=103.75 mm; Profile1_Height=430 mm; Profile1_Length=89.66 mm; Profile1_Length_2=59.77 mm; Profile_Dia=15 mm  [stored 0.0492126 ft]; Profile_Dia_2=15 mm  [stored 0.0492126 ft]; Profile_Dia_3=30 mm  [stored 0.0984252 ft]; Top_Profile=345.88 mm; Top_Profile_Ref=350.88 mm; Top_Ref=491.5 mm; Top_Ref_2=543.38 mm; W=605 mm; W_Ref=497.9 mm
- 879-0350-00-14400227290_DN350_PN16: A=249.65 mm; Body_Collar_Dia=102.08 mm; Body_Collar_Dia_2=49 mm; Body_Flange_Dia=257.89 mm; Body_Flange_Dia_2=264.86 mm; Body_Height_1=245 mm; Body_Height_2=122.5 mm; Body_Height_3=98 mm; Body_Height_4=137.5 mm; Body_Top_Dia=30.63 mm; Body_Top_Dia_2=25.52 mm; Body_With_Dia=217.78 mm; Body_With_Dia_2=217.78 mm; Bolt_support=576.47 mm; Bolt_support_2=288.24 mm; Bolt_support_Dia=30 mm  [stored 0.0984252 ft]; Bolt_support_lenght=195.07 mm; Bolt_support_lenght_2=205.07 mm; Bottom_profile=87.53 mm; D1=214.5 mm; DN=350.13 mm; FOD=260 mm; Fillet_Length=15 mm  [stored 0.0492126 ft]; Flange_thickness=26.5 mm  [stored 0.0869423 ft]; H3=875 mm; ID=175.07 mm; L=980 mm; L1=997 mm; L_Ref=988.5 mm; L_ref_2=440.17 mm; PG_Dia=110 mm; PG_Ref=163.33 mm; PG_depth=21 mm  [stored 0.0688976 ft]; PG_ref=185.07 mm; Pilot_Dia_1=60.5 mm; Pilot_Dia_1_Ref=72.6 mm; Pilot_Dia_1_Ref_2=145.2 mm; Pilot_Dia_2=102.85 mm; Pilot_Dia_3=40.33 mm; Pilot_Dia_4=20.17 mm; Pilot_Dia_5=13.44 mm; Pilot_top_1=557.75 mm; Pilot_top_ref=57.25 mm; Profile1_Height=430 mm; Profile1_Length=89.66 mm; Profile1_Length_2=59.77 mm; Profile_Dia=15 mm  [stored 0.0492126 ft]; Profile_Dia_2=15 mm  [stored 0.0492126 ft]; Profile_Dia_3=30 mm  [stored 0.0984252 ft]; Top_Profile=345.88 mm; Top_Profile_Ref=350.88 mm; Top_Ref=500.5 mm; Top_Ref_2=529.13 mm; W=605 mm; W_Ref=502.15 mm
- 879-0350-00-144002272A0_DN350_PN16: A=249.65 mm; Body_Collar_Dia=102.08 mm; Body_Collar_Dia_2=49 mm; Body_Flange_Dia=257.89 mm; Body_Flange_Dia_2=264.86 mm; Body_Height_1=245 mm; Body_Height_2=122.5 mm; Body_Height_3=98 mm; Body_Height_4=137.5 mm; Body_Top_Dia=30.63 mm; Body_Top_Dia_2=25.52 mm; Body_With_Dia=217.78 mm; Body_With_Dia_2=217.78 mm; Bolt_support=576.47 mm; Bolt_support_2=288.24 mm; Bolt_support_Dia=30 mm  [stored 0.0984252 ft]; Bolt_support_lenght=195.07 mm; Bolt_support_lenght_2=205.07 mm; Bottom_profile=87.54 mm; D1=214.5 mm; DN=350.14 mm; FOD=260 mm; Fillet_Length=15 mm  [stored 0.0492126 ft]; Flange_thickness=26.5 mm  [stored 0.0869423 ft]; H3=959 mm; ID=175.07 mm; L=980 mm; L1=997 mm; L_Ref=988.5 mm; L_ref_2=440.17 mm; PG_Dia=110 mm; PG_Ref=163.33 mm; PG_depth=21 mm  [stored 0.0688976 ft]; PG_ref=185.07 mm; Pilot_Dia_1=60.5 mm; Pilot_Dia_1_Ref=72.6 mm; Pilot_Dia_1_Ref_2=145.2 mm; Pilot_Dia_2=102.85 mm; Pilot_Dia_3=40.33 mm; Pilot_Dia_4=20.17 mm; Pilot_Dia_5=13.44 mm; Pilot_top_1=599.75 mm; Pilot_top_ref=99.25 mm; Profile1_Height=430 mm; Profile1_Length=89.66 mm; Profile1_Length_2=59.77 mm; Profile_Dia=15 mm  [stored 0.0492126 ft]; Profile_Dia_2=15 mm  [stored 0.0492126 ft]; Profile_Dia_3=30 mm  [stored 0.0984252 ft]; Top_Profile=345.88 mm; Top_Profile_Ref=350.88 mm; Top_Ref=500.5 mm; Top_Ref_2=550.13 mm; W=605 mm; W_Ref=502.15 mm
- 879-0350-00-14400237299_DN350_PN16: A=245.4 mm; Body_Collar_Dia=102.08 mm; Body_Collar_Dia_2=49 mm; Body_Flange_Dia=257.89 mm; Body_Flange_Dia_2=264.86 mm; Body_Height_1=245 mm; Body_Height_2=122.5 mm; Body_Height_3=89 mm; Body_Height_4=137.5 mm; Body_Top_Dia=30.63 mm; Body_Top_Dia_2=25.52 mm; Body_With_Dia=217.78 mm; Body_With_Dia_2=217.78 mm; Bolt_support=576.47 mm; Bolt_support_2=288.24 mm; Bolt_support_Dia=30 mm  [stored 0.0984252 ft]; Bolt_support_lenght=195.08 mm; Bolt_support_lenght_2=205.08 mm; Bottom_profile=87.54 mm; D1=214.5 mm; DN=350.15 mm; FOD=260 mm; Fillet_Length=15 mm  [stored 0.0492126 ft]; Flange_thickness=26.5 mm  [stored 0.0869423 ft]; H3=875 mm; ID=175.08 mm; L=980 mm; L1=997 mm; L_Ref=988.5 mm; L_ref_2=440.17 mm; PG_Dia=110 mm; PG_Ref=163.33 mm; PG_depth=21 mm  [stored 0.0688976 ft]; PG_ref=185.08 mm; Pilot_Dia_1=63 mm; Pilot_Dia_1_Ref=75.6 mm; Pilot_Dia_1_Ref_2=151.2 mm; Pilot_Dia_2=107.1 mm; Pilot_Dia_3=42 mm; Pilot_Dia_4=21 mm  [stored 0.0688976 ft]; Pilot_Dia_5=14 mm  [stored 0.0459318 ft]; Pilot_top_1=553.25 mm; Pilot_top_ref=61.75 mm; Profile1_Height=430 mm; Profile1_Length=89.66 mm; Profile1_Length_2=59.77 mm; Profile_Dia=15 mm  [stored 0.0492126 ft]; Profile_Dia_2=15 mm  [stored 0.0492126 ft]; Profile_Dia_3=30 mm  [stored 0.0984252 ft]; Top_Profile=345.88 mm; Top_Profile_Ref=350.88 mm; Top_Ref=491.5 mm; Top_Ref_2=522.38 mm; W=605 mm; W_Ref=497.9 mm
- 879-0350-00-144002372A0_DN350_PN16: A=245.4 mm; Body_Collar_Dia=102.08 mm; Body_Collar_Dia_2=49 mm; Body_Flange_Dia=257.89 mm; Body_Flange_Dia_2=264.86 mm; Body_Height_1=245 mm; Body_Height_2=122.5 mm; Body_Height_3=89 mm; Body_Height_4=137.5 mm; Body_Top_Dia=30.63 mm; Body_Top_Dia_2=25.52 mm; Body_With_Dia=217.78 mm; Body_With_Dia_2=217.78 mm; Bolt_support=576.47 mm; Bolt_support_2=288.24 mm; Bolt_support_Dia=30 mm  [stored 0.0984252 ft]; Bolt_support_lenght=195.08 mm; Bolt_support_lenght_2=205.08 mm; Bottom_profile=87.54 mm; D1=214.5 mm; DN=350.16 mm; FOD=260 mm; Fillet_Length=15 mm  [stored 0.0492126 ft]; Flange_thickness=26.5 mm  [stored 0.0869423 ft]; H3=959 mm; ID=175.08 mm; L=980 mm; L1=997 mm; L_Ref=988.5 mm; L_ref_2=440.17 mm; PG_Dia=110 mm; PG_Ref=163.33 mm; PG_depth=21 mm  [stored 0.0688976 ft]; PG_ref=185.08 mm; Pilot_Dia_1=63 mm; Pilot_Dia_1_Ref=75.6 mm; Pilot_Dia_1_Ref_2=151.2 mm; Pilot_Dia_2=107.1 mm; Pilot_Dia_3=42 mm; Pilot_Dia_4=21 mm  [stored 0.0688976 ft]; Pilot_Dia_5=14 mm  [stored 0.0459318 ft]; Pilot_top_1=595.25 mm; Pilot_top_ref=103.75 mm; Profile1_Height=430 mm; Profile1_Length=89.66 mm; Profile1_Length_2=59.77 mm; Profile_Dia=15 mm  [stored 0.0492126 ft]; Profile_Dia_2=15 mm  [stored 0.0492126 ft]; Profile_Dia_3=30 mm  [stored 0.0984252 ft]; Top_Profile=345.88 mm; Top_Profile_Ref=350.88 mm; Top_Ref=491.5 mm; Top_Ref_2=543.38 mm; W=605 mm; W_Ref=497.9 mm
- 879-0400-00-04400207299_DN400_PN10: A=317.7 mm; Body_Collar_Dia=114.58 mm; Body_Collar_Dia_2=55 mm; Body_Flange_Dia=289.47 mm; Body_Flange_Dia_2=297.3 mm; Body_Height_1=275 mm; Body_Height_2=137.5 mm; Body_Height_3=110 mm; Body_Height_4=152.5 mm; Body_Top_Dia=34.38 mm; Body_Top_Dia_2=28.65 mm; Body_With_Dia=244.44 mm; Body_With_Dia_2=244.44 mm; Bolt_support=647.06 mm; Bolt_support_2=323.53 mm; Bolt_support_Dia=30 mm  [stored 0.0984252 ft]; Bolt_support_lenght=220 mm; Bolt_support_lenght_2=230 mm; Bottom_profile=100 mm; D1=240 mm; DN=400 mm; FOD=282.5 mm; Fillet_Length=20 mm  [stored 0.0656168 ft]; Flange_thickness=28 mm  [stored 0.0918635 ft]; H3=1000 mm; ID=200 mm; L=1100 mm; L1=1117 mm; L_Ref=1108.5 mm; L_ref_2=495.81 mm; PG_Dia=110 mm; PG_Ref=183.33 mm; PG_depth=21 mm  [stored 0.0688976 ft]; PG_ref=210 mm; Pilot_Dia_1=69 mm; Pilot_Dia_1_Ref=82.8 mm; Pilot_Dia_1_Ref_2=165.6 mm; Pilot_Dia_2=117.3 mm; Pilot_Dia_3=46 mm; Pilot_Dia_4=23 mm; Pilot_Dia_5=15.33 mm; Pilot_top_1=637.5 mm; Pilot_top_ref=80 mm; Profile1_Height=480 mm; Profile1_Length=97.41 mm; Profile1_Length_2=64.94 mm; Profile_Dia=15 mm  [stored 0.0492126 ft]; Profile_Dia_2=15 mm  [stored 0.0492126 ft]; Profile_Dia_3=30 mm  [stored 0.0984252 ft]; Top_Profile=388.24 mm; Top_Profile_Ref=393.24 mm; Top_Ref=557.5 mm; Top_Ref_2=597.5 mm; W=710 mm; W_Ref=592.7 mm
- 879-0400-00-044002072A0_DN400_PN10: A=317.7 mm; Body_Collar_Dia=114.58 mm; Body_Collar_Dia_2=55 mm; Body_Flange_Dia=289.47 mm; Body_Flange_Dia_2=297.3 mm; Body_Height_1=275 mm; Body_Height_2=137.5 mm; Body_Height_3=122 mm; Body_Height_4=152.5 mm; Body_Top_Dia=34.38 mm; Body_Top_Dia_2=28.65 mm; Body_With_Dia=244.44 mm; Body_With_Dia_2=244.44 mm; Bolt_support=647.06 mm; Bolt_support_2=323.53 mm; Bolt_support_Dia=30 mm  [stored 0.0984252 ft]; Bolt_support_lenght=220.05 mm; Bolt_support_lenght_2=230.05 mm; Bottom_profile=100.03 mm; D1=240 mm; DN=400.1 mm; FOD=282.5 mm; Fillet_Length=20 mm  [stored 0.0656168 ft]; Flange_thickness=28 mm  [stored 0.0918635 ft]; H3=1159 mm; ID=200.05 mm; L=1100 mm; L1=1117 mm; L_Ref=1108.5 mm; L_ref_2=495.81 mm; PG_Dia=110 mm; PG_Ref=183.33 mm; PG_depth=21 mm  [stored 0.0688976 ft]; PG_ref=210.05 mm; Pilot_Dia_1=69 mm; Pilot_Dia_1_Ref=82.8 mm; Pilot_Dia_1_Ref_2=165.6 mm; Pilot_Dia_2=117.3 mm; Pilot_Dia_3=46 mm; Pilot_Dia_4=23 mm; Pilot_Dia_5=15.33 mm; Pilot_top_1=723 mm; Pilot_top_ref=153.5 mm; Profile1_Height=480 mm; Profile1_Length=97.41 mm; Profile1_Length_2=64.94 mm; Profile_Dia=15 mm  [stored 0.0492126 ft]; Profile_Dia_2=15 mm  [stored 0.0492126 ft]; Profile_Dia_3=30 mm  [stored 0.0984252 ft]; Top_Profile=388.24 mm; Top_Profile_Ref=393.24 mm; Top_Ref=569.5 mm; Top_Ref_2=646.25 mm; W=710 mm; W_Ref=592.7 mm
- 879-0400-00-04400217299_DN400_PN10: A=314.3 mm; Body_Collar_Dia=114.58 mm; Body_Collar_Dia_2=55 mm; Body_Flange_Dia=289.47 mm; Body_Flange_Dia_2=297.3 mm; Body_Height_1=275 mm; Body_Height_2=137.5 mm; Body_Height_3=100 mm; Body_Height_4=152.5 mm; Body_Top_Dia=34.38 mm; Body_Top_Dia_2=28.65 mm; Body_With_Dia=244.44 mm; Body_With_Dia_2=244.44 mm; Bolt_support=647.06 mm; Bolt_support_2=323.53 mm; Bolt_support_Dia=30 mm  [stored 0.0984252 ft]; Bolt_support_lenght=220.1 mm; Bolt_support_lenght_2=230.1 mm; Bottom_profile=100.05 mm; D1=240 mm; DN=400.2 mm; FOD=282.5 mm; Fillet_Length=20 mm  [stored 0.0656168 ft]; Flange_thickness=28 mm  [stored 0.0918635 ft]; H3=1000 mm; ID=200.1 mm; L=1100 mm; L1=1117 mm; L_Ref=1108.5 mm; L_ref_2=495.81 mm; PG_Dia=110 mm; PG_Ref=183.33 mm; PG_depth=21 mm  [stored 0.0688976 ft]; PG_ref=210.1 mm; Pilot_Dia_1=71 mm; Pilot_Dia_1_Ref=85.2 mm; Pilot_Dia_1_Ref_2=170.4 mm; Pilot_Dia_2=120.7 mm; Pilot_Dia_3=47.33 mm; Pilot_Dia_4=23.67 mm; Pilot_Dia_5=15.78 mm; Pilot_top_1=632.5 mm; Pilot_top_ref=85 mm; Profile1_Height=480 mm; Profile1_Length=97.41 mm; Profile1_Length_2=64.94 mm; Profile_Dia=15 mm  [stored 0.0492126 ft]; Profile_Dia_2=15 mm  [stored 0.0492126 ft]; Profile_Dia_3=30 mm  [stored 0.0984252 ft]; Top_Profile=388.24 mm; Top_Profile_Ref=393.24 mm; Top_Ref=547.5 mm; Top_Ref_2=590 mm; W=710 mm; W_Ref=589.3 mm
- 879-0400-00-044002172A0_DN400_PN10: A=314.3 mm; Body_Collar_Dia=114.58 mm; Body_Collar_Dia_2=55 mm; Body_Flange_Dia=289.47 mm; Body_Flange_Dia_2=297.3 mm; Body_Height_1=275 mm; Body_Height_2=137.5 mm; Body_Height_3=110 mm; Body_Height_4=152.5 mm; Body_Top_Dia=34.38 mm; Body_Top_Dia_2=28.65 mm; Body_With_Dia=244.44 mm; Body_With_Dia_2=244.44 mm; Bolt_support=647.06 mm; Bolt_support_2=323.53 mm; Bolt_support_Dia=30 mm  [stored 0.0984252 ft]; Bolt_support_lenght=220.15 mm; Bolt_support_lenght_2=230.15 mm; Bottom_profile=100.08 mm; D1=240 mm; DN=400.3 mm; FOD=282.5 mm; Fillet_Length=20 mm  [stored 0.0656168 ft]; Flange_thickness=28 mm  [stored 0.0918635 ft]; H3=1159 mm; ID=200.15 mm; L=1100 mm; L1=1117 mm; L_Ref=1108.5 mm; L_ref_2=495.81 mm; PG_Dia=110 mm; PG_Ref=183.33 mm; PG_depth=21 mm  [stored 0.0688976 ft]; PG_ref=210.15 mm; Pilot_Dia_1=71 mm; Pilot_Dia_1_Ref=85.2 mm; Pilot_Dia_1_Ref_2=170.4 mm; Pilot_Dia_2=120.7 mm; Pilot_Dia_3=47.33 mm; Pilot_Dia_4=23.67 mm; Pilot_Dia_5=15.78 mm; Pilot_top_1=717 mm; Pilot_top_ref=159.5 mm; Profile1_Height=480 mm; Profile1_Length=97.41 mm; Profile1_Length_2=64.94 mm; Profile_Dia=15 mm  [stored 0.0492126 ft]; Profile_Dia_2=15 mm  [stored 0.0492126 ft]; Profile_Dia_3=30 mm  [stored 0.0984252 ft]; Top_Profile=388.24 mm; Top_Profile_Ref=393.24 mm; Top_Ref=557.5 mm; Top_Ref_2=637.25 mm; W=710 mm; W_Ref=589.3 mm
- 879-0400-00-04400227299_DN400_PN10: A=317.7 mm; Body_Collar_Dia=114.58 mm; Body_Collar_Dia_2=55 mm; Body_Flange_Dia=289.47 mm; Body_Flange_Dia_2=297.3 mm; Body_Height_1=275 mm; Body_Height_2=137.5 mm; Body_Height_3=110 mm; Body_Height_4=152.5 mm; Body_Top_Dia=34.38 mm; Body_Top_Dia_2=28.65 mm; Body_With_Dia=244.44 mm; Body_With_Dia_2=244.44 mm; Bolt_support=647.06 mm; Bolt_support_2=323.53 mm; Bolt_support_Dia=30 mm  [stored 0.0984252 ft]; Bolt_support_lenght=220.2 mm; Bolt_support_lenght_2=230.2 mm; Bottom_profile=100.1 mm; D1=240 mm; DN=400.4 mm; FOD=282.5 mm; Fillet_Length=20 mm  [stored 0.0656168 ft]; Flange_thickness=28 mm  [stored 0.0918635 ft]; H3=1000 mm; ID=200.2 mm; L=1100 mm; L1=1117 mm; L_Ref=1108.5 mm; L_ref_2=495.81 mm; PG_Dia=110 mm; PG_Ref=183.33 mm; PG_depth=21 mm  [stored 0.0688976 ft]; PG_ref=210.2 mm; Pilot_Dia_1=69 mm; Pilot_Dia_1_Ref=82.8 mm; Pilot_Dia_1_Ref_2=165.6 mm; Pilot_Dia_2=117.3 mm; Pilot_Dia_3=46 mm; Pilot_Dia_4=23 mm; Pilot_Dia_5=15.33 mm; Pilot_top_1=637.5 mm; Pilot_top_ref=80 mm; Profile1_Height=480 mm; Profile1_Length=97.41 mm; Profile1_Length_2=64.94 mm; Profile_Dia=15 mm  [stored 0.0492126 ft]; Profile_Dia_2=15 mm  [stored 0.0492126 ft]; Profile_Dia_3=30 mm  [stored 0.0984252 ft]; Top_Profile=388.24 mm; Top_Profile_Ref=393.24 mm; Top_Ref=557.5 mm; Top_Ref_2=597.5 mm; W=710 mm; W_Ref=592.7 mm
- 879-0400-00-044002272A0_DN400_PN10: A=317.7 mm; Body_Collar_Dia=114.58 mm; Body_Collar_Dia_2=55 mm; Body_Flange_Dia=289.47 mm; Body_Flange_Dia_2=297.3 mm; Body_Height_1=275 mm; Body_Height_2=137.5 mm; Body_Height_3=122 mm; Body_Height_4=152.5 mm; Body_Top_Dia=34.38 mm; Body_Top_Dia_2=28.65 mm; Body_With_Dia=244.44 mm; Body_With_Dia_2=244.44 mm; Bolt_support=647.06 mm; Bolt_support_2=323.53 mm; Bolt_support_Dia=30 mm  [stored 0.0984252 ft]; Bolt_support_lenght=220.25 mm; Bolt_support_lenght_2=230.25 mm; Bottom_profile=100.13 mm; D1=240 mm; DN=400.5 mm; FOD=282.5 mm; Fillet_Length=20 mm  [stored 0.0656168 ft]; Flange_thickness=28 mm  [stored 0.0918635 ft]; H3=1159 mm; ID=200.25 mm; L=1100 mm; L1=1117 mm; L_Ref=1108.5 mm; L_ref_2=495.81 mm; PG_Dia=110 mm; PG_Ref=183.33 mm; PG_depth=21 mm  [stored 0.0688976 ft]; PG_ref=210.25 mm; Pilot_Dia_1=69 mm; Pilot_Dia_1_Ref=82.8 mm; Pilot_Dia_1_Ref_2=165.6 mm; Pilot_Dia_2=117.3 mm; Pilot_Dia_3=46 mm; Pilot_Dia_4=23 mm; Pilot_Dia_5=15.33 mm; Pilot_top_1=723 mm; Pilot_top_ref=153.5 mm; Profile1_Height=480 mm; Profile1_Length=97.41 mm; Profile1_Length_2=64.94 mm; Profile_Dia=15 mm  [stored 0.0492126 ft]; Profile_Dia_2=15 mm  [stored 0.0492126 ft]; Profile_Dia_3=30 mm  [stored 0.0984252 ft]; Top_Profile=388.24 mm; Top_Profile_Ref=393.24 mm; Top_Ref=569.5 mm; Top_Ref_2=646.25 mm; W=710 mm; W_Ref=592.7 mm
- 879-0400-00-04400237299_DN400_PN10: A=314.3 mm; Body_Collar_Dia=114.58 mm; Body_Collar_Dia_2=55 mm; Body_Flange_Dia=289.47 mm; Body_Flange_Dia_2=297.3 mm; Body_Height_1=275 mm; Body_Height_2=137.5 mm; Body_Height_3=100 mm; Body_Height_4=152.5 mm; Body_Top_Dia=34.38 mm; Body_Top_Dia_2=28.65 mm; Body_With_Dia=244.44 mm; Body_With_Dia_2=244.44 mm; Bolt_support=647.06 mm; Bolt_support_2=323.53 mm; Bolt_support_Dia=30 mm  [stored 0.0984252 ft]; Bolt_support_lenght=220.3 mm; Bolt_support_lenght_2=230.3 mm; Bottom_profile=100.15 mm; D1=240 mm; DN=400.6 mm; FOD=282.5 mm; Fillet_Length=20 mm  [stored 0.0656168 ft]; Flange_thickness=28 mm  [stored 0.0918635 ft]; H3=1000 mm; ID=200.3 mm; L=1100 mm; L1=1117 mm; L_Ref=1108.5 mm; L_ref_2=495.81 mm; PG_Dia=110 mm; PG_Ref=183.33 mm; PG_depth=21 mm  [stored 0.0688976 ft]; PG_ref=210.3 mm; Pilot_Dia_1=71 mm; Pilot_Dia_1_Ref=85.2 mm; Pilot_Dia_1_Ref_2=170.4 mm; Pilot_Dia_2=120.7 mm; Pilot_Dia_3=47.33 mm; Pilot_Dia_4=23.67 mm; Pilot_Dia_5=15.78 mm; Pilot_top_1=632.5 mm; Pilot_top_ref=85 mm; Profile1_Height=480 mm; Profile1_Length=97.41 mm; Profile1_Length_2=64.94 mm; Profile_Dia=15 mm  [stored 0.0492126 ft]; Profile_Dia_2=15 mm  [stored 0.0492126 ft]; Profile_Dia_3=30 mm  [stored 0.0984252 ft]; Top_Profile=388.24 mm; Top_Profile_Ref=393.24 mm; Top_Ref=547.5 mm; Top_Ref_2=590 mm; W=710 mm; W_Ref=589.3 mm
- 879-0400-00-044002372A0_DN400_PN10: A=314.3 mm; Body_Collar_Dia=114.58 mm; Body_Collar_Dia_2=55 mm; Body_Flange_Dia=289.47 mm; Body_Flange_Dia_2=297.3 mm; Body_Height_1=275 mm; Body_Height_2=137.5 mm; Body_Height_3=110 mm; Body_Height_4=152.5 mm; Body_Top_Dia=34.38 mm; Body_Top_Dia_2=28.65 mm; Body_With_Dia=244.44 mm; Body_With_Dia_2=244.44 mm; Bolt_support=647.06 mm; Bolt_support_2=323.53 mm; Bolt_support_Dia=30 mm  [stored 0.0984252 ft]; Bolt_support_lenght=220.35 mm; Bolt_support_lenght_2=230.35 mm; Bottom_profile=100.18 mm; D1=240 mm; DN=400.7 mm; FOD=282.5 mm; Fillet_Length=20 mm  [stored 0.0656168 ft]; Flange_thickness=28 mm  [stored 0.0918635 ft]; H3=1159 mm; ID=200.35 mm; L=1100 mm; L1=1117 mm; L_Ref=1108.5 mm; L_ref_2=495.81 mm; PG_Dia=110 mm; PG_Ref=183.33 mm; PG_depth=21 mm  [stored 0.0688976 ft]; PG_ref=210.35 mm; Pilot_Dia_1=71 mm; Pilot_Dia_1_Ref=85.2 mm; Pilot_Dia_1_Ref_2=170.4 mm; Pilot_Dia_2=120.7 mm; Pilot_Dia_3=47.33 mm; Pilot_Dia_4=23.67 mm; Pilot_Dia_5=15.78 mm; Pilot_top_1=717 mm; Pilot_top_ref=159.5 mm; Profile1_Height=480 mm; Profile1_Length=97.41 mm; Profile1_Length_2=64.94 mm; Profile_Dia=15 mm  [stored 0.0492126 ft]; Profile_Dia_2=15 mm  [stored 0.0492126 ft]; Profile_Dia_3=30 mm  [stored 0.0984252 ft]; Top_Profile=388.24 mm; Top_Profile_Ref=393.24 mm; Top_Ref=557.5 mm; Top_Ref_2=637.25 mm; W=710 mm; W_Ref=589.3 mm
- 879-0400-00-14400207290_DN400_PN16: A=310.2 mm; Body_Collar_Dia=114.58 mm; Body_Collar_Dia_2=55 mm; Body_Flange_Dia=289.47 mm; Body_Flange_Dia_2=297.3 mm; Body_Height_1=275 mm; Body_Height_2=137.5 mm; Body_Height_3=110 mm; Body_Height_4=152.5 mm; Body_Top_Dia=34.38 mm; Body_Top_Dia_2=28.65 mm; Body_With_Dia=244.44 mm; Body_With_Dia_2=244.44 mm; Bolt_support=647.06 mm; Bolt_support_2=323.53 mm; Bolt_support_Dia=30 mm  [stored 0.0984252 ft]; Bolt_support_lenght=220.4 mm; Bolt_support_lenght_2=230.4 mm; Bottom_profile=100.2 mm; D1=240 mm; DN=400.8 mm; FOD=290 mm; Fillet_Length=20 mm  [stored 0.0656168 ft]; Flange_thickness=28 mm  [stored 0.0918635 ft]; H3=1000 mm; ID=200.4 mm; L=1100 mm; L1=1117 mm; L_Ref=1108.5 mm; L_ref_2=495.81 mm; PG_Dia=110 mm; PG_Ref=183.33 mm; PG_depth=21 mm  [stored 0.0688976 ft]; PG_ref=210.4 mm; Pilot_Dia_1=69 mm; Pilot_Dia_1_Ref=82.8 mm; Pilot_Dia_1_Ref_2=165.6 mm; Pilot_Dia_2=117.3 mm; Pilot_Dia_3=46 mm; Pilot_Dia_4=23 mm; Pilot_Dia_5=15.33 mm; Pilot_top_1=633.75 mm; Pilot_top_ref=76.25 mm; Profile1_Height=480 mm; Profile1_Length=100 mm; Profile1_Length_2=66.67 mm; Profile_Dia=15 mm  [stored 0.0492126 ft]; Profile_Dia_2=15 mm  [stored 0.0492126 ft]; Profile_Dia_3=30 mm  [stored 0.0984252 ft]; Top_Profile=388.24 mm; Top_Profile_Ref=393.24 mm; Top_Ref=557.5 mm; Top_Ref_2=595.63 mm; W=710 mm; W_Ref=592.7 mm
- 879-0400-00-144002072A0_DN400_PN16: A=310.2 mm; Body_Collar_Dia=114.58 mm; Body_Collar_Dia_2=55 mm; Body_Flange_Dia=289.47 mm; Body_Flange_Dia_2=297.3 mm; Body_Height_1=275 mm; Body_Height_2=137.5 mm; Body_Height_3=122 mm; Body_Height_4=152.5 mm; Body_Top_Dia=34.38 mm; Body_Top_Dia_2=28.65 mm; Body_With_Dia=244.44 mm; Body_With_Dia_2=244.44 mm; Bolt_support=647.06 mm; Bolt_support_2=323.53 mm; Bolt_support_Dia=30 mm  [stored 0.0984252 ft]; Bolt_support_lenght=220.45 mm; Bolt_support_lenght_2=230.45 mm; Bottom_profile=100.23 mm; D1=240 mm; DN=400.9 mm; FOD=290 mm; Fillet_Length=20 mm  [stored 0.0656168 ft]; Flange_thickness=28 mm  [stored 0.0918635 ft]; H3=1159 mm; ID=200.45 mm; L=1100 mm; L1=1117 mm; L_Ref=1108.5 mm; L_ref_2=495.81 mm; PG_Dia=110 mm; PG_Ref=183.33 mm; PG_depth=21 mm  [stored 0.0688976 ft]; PG_ref=210.45 mm; Pilot_Dia_1=69 mm; Pilot_Dia_1_Ref=82.8 mm; Pilot_Dia_1_Ref_2=165.6 mm; Pilot_Dia_2=117.3 mm; Pilot_Dia_3=46 mm; Pilot_Dia_4=23 mm; Pilot_Dia_5=15.33 mm; Pilot_top_1=719.25 mm; Pilot_top_ref=149.75 mm; Profile1_Height=480 mm; Profile1_Length=100 mm; Profile1_Length_2=66.67 mm; Profile_Dia=15 mm  [stored 0.0492126 ft]; Profile_Dia_2=15 mm  [stored 0.0492126 ft]; Profile_Dia_3=30 mm  [stored 0.0984252 ft]; Top_Profile=388.24 mm; Top_Profile_Ref=393.24 mm; Top_Ref=569.5 mm; Top_Ref_2=644.38 mm; W=710 mm; W_Ref=592.7 mm
- 879-0400-00-14400217299_DN400_PN16: A=306.8 mm; Body_Collar_Dia=114.58 mm; Body_Collar_Dia_2=55 mm; Body_Flange_Dia=289.47 mm; Body_Flange_Dia_2=297.3 mm; Body_Height_1=275 mm; Body_Height_2=137.5 mm; Body_Height_3=100 mm; Body_Height_4=152.5 mm; Body_Top_Dia=34.38 mm; Body_Top_Dia_2=28.65 mm; Body_With_Dia=244.44 mm; Body_With_Dia_2=244.44 mm; Bolt_support=647.06 mm; Bolt_support_2=323.53 mm; Bolt_support_Dia=30 mm  [stored 0.0984252 ft]; Bolt_support_lenght=220.06 mm; Bolt_support_lenght_2=230.06 mm; Bottom_profile=100.03 mm; D1=240 mm; DN=400.11 mm; FOD=290 mm; Fillet_Length=20 mm  [stored 0.0656168 ft]; Flange_thickness=28 mm  [stored 0.0918635 ft]; H3=1000 mm; ID=200.06 mm; L=1100 mm; L1=1117 mm; L_Ref=1108.5 mm; L_ref_2=495.81 mm; PG_Dia=110 mm; PG_Ref=183.33 mm; PG_depth=21 mm  [stored 0.0688976 ft]; PG_ref=210.06 mm; Pilot_Dia_1=71 mm; Pilot_Dia_1_Ref=85.2 mm; Pilot_Dia_1_Ref_2=170.4 mm; Pilot_Dia_2=120.7 mm; Pilot_Dia_3=47.33 mm; Pilot_Dia_4=23.67 mm; Pilot_Dia_5=15.78 mm; Pilot_top_1=628.75 mm; Pilot_top_ref=81.25 mm; Profile1_Height=480 mm; Profile1_Length=100 mm; Profile1_Length_2=66.67 mm; Profile_Dia=15 mm  [stored 0.0492126 ft]; Profile_Dia_2=15 mm  [stored 0.0492126 ft]; Profile_Dia_3=30 mm  [stored 0.0984252 ft]; Top_Profile=388.24 mm; Top_Profile_Ref=393.24 mm; Top_Ref=547.5 mm; Top_Ref_2=588.13 mm; W=710 mm; W_Ref=589.3 mm
- 879-0400-00-144002172A0_DN400_PN16: A=306.8 mm; Body_Collar_Dia=114.58 mm; Body_Collar_Dia_2=55 mm; Body_Flange_Dia=289.47 mm; Body_Flange_Dia_2=297.3 mm; Body_Height_1=275 mm; Body_Height_2=137.5 mm; Body_Height_3=110 mm; Body_Height_4=152.5 mm; Body_Top_Dia=34.38 mm; Body_Top_Dia_2=28.65 mm; Body_With_Dia=244.44 mm; Body_With_Dia_2=244.44 mm; Bolt_support=647.06 mm; Bolt_support_2=323.53 mm; Bolt_support_Dia=30 mm  [stored 0.0984252 ft]; Bolt_support_lenght=220.06 mm; Bolt_support_lenght_2=230.06 mm; Bottom_profile=100.03 mm; D1=240 mm; DN=400.12 mm; FOD=290 mm; Fillet_Length=20 mm  [stored 0.0656168 ft]; Flange_thickness=28 mm  [stored 0.0918635 ft]; H3=1159 mm; ID=200.06 mm; L=1100 mm; L1=1117 mm; L_Ref=1108.5 mm; L_ref_2=495.81 mm; PG_Dia=110 mm; PG_Ref=183.33 mm; PG_depth=21 mm  [stored 0.0688976 ft]; PG_ref=210.06 mm; Pilot_Dia_1=71 mm; Pilot_Dia_1_Ref=85.2 mm; Pilot_Dia_1_Ref_2=170.4 mm; Pilot_Dia_2=120.7 mm; Pilot_Dia_3=47.33 mm; Pilot_Dia_4=23.67 mm; Pilot_Dia_5=15.78 mm; Pilot_top_1=713.25 mm; Pilot_top_ref=155.75 mm; Profile1_Height=480 mm; Profile1_Length=100 mm; Profile1_Length_2=66.67 mm; Profile_Dia=15 mm  [stored 0.0492126 ft]; Profile_Dia_2=15 mm  [stored 0.0492126 ft]; Profile_Dia_3=30 mm  [stored 0.0984252 ft]; Top_Profile=388.24 mm; Top_Profile_Ref=393.24 mm; Top_Ref=557.5 mm; Top_Ref_2=635.38 mm; W=710 mm; W_Ref=589.3 mm
- 879-0400-00-14400227299_DN400_PN16: A=310.2 mm; Body_Collar_Dia=114.58 mm; Body_Collar_Dia_2=55 mm; Body_Flange_Dia=289.47 mm; Body_Flange_Dia_2=297.3 mm; Body_Height_1=275 mm; Body_Height_2=137.5 mm; Body_Height_3=110 mm; Body_Height_4=152.5 mm; Body_Top_Dia=34.38 mm; Body_Top_Dia_2=28.65 mm; Body_With_Dia=244.44 mm; Body_With_Dia_2=244.44 mm; Bolt_support=647.06 mm; Bolt_support_2=323.53 mm; Bolt_support_Dia=30 mm  [stored 0.0984252 ft]; Bolt_support_lenght=220.07 mm; Bolt_support_lenght_2=230.07 mm; Bottom_profile=100.03 mm; D1=240 mm; DN=400.13 mm; FOD=290 mm; Fillet_Length=20 mm  [stored 0.0656168 ft]; Flange_thickness=28 mm  [stored 0.0918635 ft]; H3=1000 mm; ID=200.07 mm; L=1100 mm; L1=1117 mm; L_Ref=1108.5 mm; L_ref_2=495.81 mm; PG_Dia=110 mm; PG_Ref=183.33 mm; PG_depth=21 mm  [stored 0.0688976 ft]; PG_ref=210.07 mm; Pilot_Dia_1=69 mm; Pilot_Dia_1_Ref=82.8 mm; Pilot_Dia_1_Ref_2=165.6 mm; Pilot_Dia_2=117.3 mm; Pilot_Dia_3=46 mm; Pilot_Dia_4=23 mm; Pilot_Dia_5=15.33 mm; Pilot_top_1=633.75 mm; Pilot_top_ref=76.25 mm; Profile1_Height=480 mm; Profile1_Length=100 mm; Profile1_Length_2=66.67 mm; Profile_Dia=15 mm  [stored 0.0492126 ft]; Profile_Dia_2=15 mm  [stored 0.0492126 ft]; Profile_Dia_3=30 mm  [stored 0.0984252 ft]; Top_Profile=388.24 mm; Top_Profile_Ref=393.24 mm; Top_Ref=557.5 mm; Top_Ref_2=595.63 mm; W=710 mm; W_Ref=592.7 mm
- 879-0400-00-144002272A0_DN400_PN16: A=310.2 mm; Body_Collar_Dia=114.58 mm; Body_Collar_Dia_2=55 mm; Body_Flange_Dia=289.47 mm; Body_Flange_Dia_2=297.3 mm; Body_Height_1=275 mm; Body_Height_2=137.5 mm; Body_Height_3=122 mm; Body_Height_4=152.5 mm; Body_Top_Dia=34.38 mm; Body_Top_Dia_2=28.65 mm; Body_With_Dia=244.44 mm; Body_With_Dia_2=244.44 mm; Bolt_support=647.06 mm; Bolt_support_2=323.53 mm; Bolt_support_Dia=30 mm  [stored 0.0984252 ft]; Bolt_support_lenght=220.07 mm; Bolt_support_lenght_2=230.07 mm; Bottom_profile=100.04 mm; D1=240 mm; DN=400.14 mm; FOD=290 mm; Fillet_Length=20 mm  [stored 0.0656168 ft]; Flange_thickness=28 mm  [stored 0.0918635 ft]; H3=1159 mm; ID=200.07 mm; L=1100 mm; L1=1117 mm; L_Ref=1108.5 mm; L_ref_2=495.81 mm; PG_Dia=110 mm; PG_Ref=183.33 mm; PG_depth=21 mm  [stored 0.0688976 ft]; PG_ref=210.07 mm; Pilot_Dia_1=69 mm; Pilot_Dia_1_Ref=82.8 mm; Pilot_Dia_1_Ref_2=165.6 mm; Pilot_Dia_2=117.3 mm; Pilot_Dia_3=46 mm; Pilot_Dia_4=23 mm; Pilot_Dia_5=15.33 mm; Pilot_top_1=719.25 mm; Pilot_top_ref=149.75 mm; Profile1_Height=480 mm; Profile1_Length=100 mm; Profile1_Length_2=66.67 mm; Profile_Dia=15 mm  [stored 0.0492126 ft]; Profile_Dia_2=15 mm  [stored 0.0492126 ft]; Profile_Dia_3=30 mm  [stored 0.0984252 ft]; Top_Profile=388.24 mm; Top_Profile_Ref=393.24 mm; Top_Ref=569.5 mm; Top_Ref_2=644.38 mm; W=710 mm; W_Ref=592.7 mm
- 879-0400-00-14400237299_DN400_PN16: A=306.8 mm; Body_Collar_Dia=114.58 mm; Body_Collar_Dia_2=55 mm; Body_Flange_Dia=289.47 mm; Body_Flange_Dia_2=297.3 mm; Body_Height_1=275 mm; Body_Height_2=137.5 mm; Body_Height_3=100 mm; Body_Height_4=152.5 mm; Body_Top_Dia=34.38 mm; Body_Top_Dia_2=28.65 mm; Body_With_Dia=244.44 mm; Body_With_Dia_2=244.44 mm; Bolt_support=647.06 mm; Bolt_support_2=323.53 mm; Bolt_support_Dia=30 mm  [stored 0.0984252 ft]; Bolt_support_lenght=220.08 mm; Bolt_support_lenght_2=230.08 mm; Bottom_profile=100.04 mm; D1=240 mm; DN=400.15 mm; FOD=290 mm; Fillet_Length=20 mm  [stored 0.0656168 ft]; Flange_thickness=28 mm  [stored 0.0918635 ft]; H3=1000 mm; ID=200.08 mm; L=1100 mm; L1=1117 mm; L_Ref=1108.5 mm; L_ref_2=495.81 mm; PG_Dia=110 mm; PG_Ref=183.33 mm; PG_depth=21 mm  [stored 0.0688976 ft]; PG_ref=210.08 mm; Pilot_Dia_1=71 mm; Pilot_Dia_1_Ref=85.2 mm; Pilot_Dia_1_Ref_2=170.4 mm; Pilot_Dia_2=120.7 mm; Pilot_Dia_3=47.33 mm; Pilot_Dia_4=23.67 mm; Pilot_Dia_5=15.78 mm; Pilot_top_1=628.75 mm; Pilot_top_ref=81.25 mm; Profile1_Height=480 mm; Profile1_Length=100 mm; Profile1_Length_2=66.67 mm; Profile_Dia=15 mm  [stored 0.0492126 ft]; Profile_Dia_2=15 mm  [stored 0.0492126 ft]; Profile_Dia_3=30 mm  [stored 0.0984252 ft]; Top_Profile=388.24 mm; Top_Profile_Ref=393.24 mm; Top_Ref=547.5 mm; Top_Ref_2=588.13 mm; W=710 mm; W_Ref=589.3 mm
- 879-0400-00-144002372A0_DN400_PN16: A=306.8 mm; Body_Collar_Dia=114.58 mm; Body_Collar_Dia_2=55 mm; Body_Flange_Dia=289.47 mm; Body_Flange_Dia_2=297.3 mm; Body_Height_1=275 mm; Body_Height_2=137.5 mm; Body_Height_3=110 mm; Body_Height_4=152.5 mm; Body_Top_Dia=34.38 mm; Body_Top_Dia_2=28.65 mm; Body_With_Dia=244.44 mm; Body_With_Dia_2=244.44 mm; Bolt_support=647.06 mm; Bolt_support_2=323.53 mm; Bolt_support_Dia=30 mm  [stored 0.0984252 ft]; Bolt_support_lenght=220.08 mm; Bolt_support_lenght_2=230.08 mm; Bottom_profile=100.04 mm; D1=240 mm; DN=400.16 mm; FOD=290 mm; Fillet_Length=20 mm  [stored 0.0656168 ft]; Flange_thickness=28 mm  [stored 0.0918635 ft]; H3=1159 mm; ID=200.08 mm; L=1100 mm; L1=1117 mm; L_Ref=1108.5 mm; L_ref_2=495.81 mm; PG_Dia=110 mm; PG_Ref=183.33 mm; PG_depth=21 mm  [stored 0.0688976 ft]; PG_ref=210.08 mm; Pilot_Dia_1=71 mm; Pilot_Dia_1_Ref=85.2 mm; Pilot_Dia_1_Ref_2=170.4 mm; Pilot_Dia_2=120.7 mm; Pilot_Dia_3=47.33 mm; Pilot_Dia_4=23.67 mm; Pilot_Dia_5=15.78 mm; Pilot_top_1=713.25 mm; Pilot_top_ref=155.75 mm; Profile1_Height=480 mm; Profile1_Length=100 mm; Profile1_Length_2=66.67 mm; Profile_Dia=15 mm  [stored 0.0492126 ft]; Profile_Dia_2=15 mm  [stored 0.0492126 ft]; Profile_Dia_3=30 mm  [stored 0.0984252 ft]; Top_Profile=388.24 mm; Top_Profile_Ref=393.24 mm; Top_Ref=557.5 mm; Top_Ref_2=635.38 mm; W=710 mm; W_Ref=589.3 mm
- 879-0250-00-044002372A0_DN250_PN10: A=237.6 mm; Body_Collar_Dia=76.04 mm; Body_Collar_Dia_2=36.5 mm; Body_Flange_Dia=192.11 mm; Body_Flange_Dia_2=197.3 mm; Body_Height_1=182.5 mm; Body_Height_2=91.25 mm; Body_Height_3=81 mm; Body_Height_4=106.25 mm; Body_Top_Dia=22.81 mm; Body_Top_Dia_2=19.01 mm; Body_With_Dia=162.22 mm; Body_With_Dia_2=162.22 mm; Bolt_support=429.41 mm; Bolt_support_2=214.71 mm; Bolt_support_Dia=20 mm  [stored 0.0656168 ft]; Bolt_support_lenght=145.35 mm; Bolt_support_lenght_2=155.35 mm; Bottom_profile=62.68 mm; D1=159.5 mm; DN=250.7 mm; FOD=197.5 mm; Fillet_Length=10 mm  [stored 0.0328084 ft]; Flange_thickness=22 mm  [stored 0.0721785 ft]; H3=806 mm; ID=125.35 mm; L=730 mm; L1=747 mm; L_Ref=738.5 mm; L_ref_2=325.62 mm; PG_Dia=80 mm; PG_Ref=121.67 mm; PG_depth=14 mm  [stored 0.0459318 ft]; PG_ref=135.35 mm; Pilot_Dia_1=47 mm; Pilot_Dia_1_Ref=56.4 mm; Pilot_Dia_1_Ref_2=112.8 mm; Pilot_Dia_2=79.9 mm; Pilot_Dia_3=31.33 mm; Pilot_Dia_4=15.67 mm; Pilot_Dia_5=10.44 mm; Pilot_top_1=499.13 mm; Pilot_top_ref=109.38 mm; Profile1_Height=350 mm; Profile1_Length=68.1 mm; Profile1_Length_2=45.4 mm; Profile_Dia=10 mm  [stored 0.0328084 ft]; Profile_Dia_2=10 mm  [stored 0.0328084 ft]; Profile_Dia_3=20 mm  [stored 0.0656168 ft]; Top_Profile=257.65 mm; Top_Profile_Ref=262.65 mm; Top_Ref=389.75 mm; Top_Ref_2=444.44 mm; W=510 mm; W_Ref=430.1 mm

note: [stored X ft] marks values corroborated as IEEE doubles in the binary element streams (Revit-internal decimal feet)

## geometry (parser evidence)
native form markers: Sweep x6
no freeform markers — native parametric forms only
